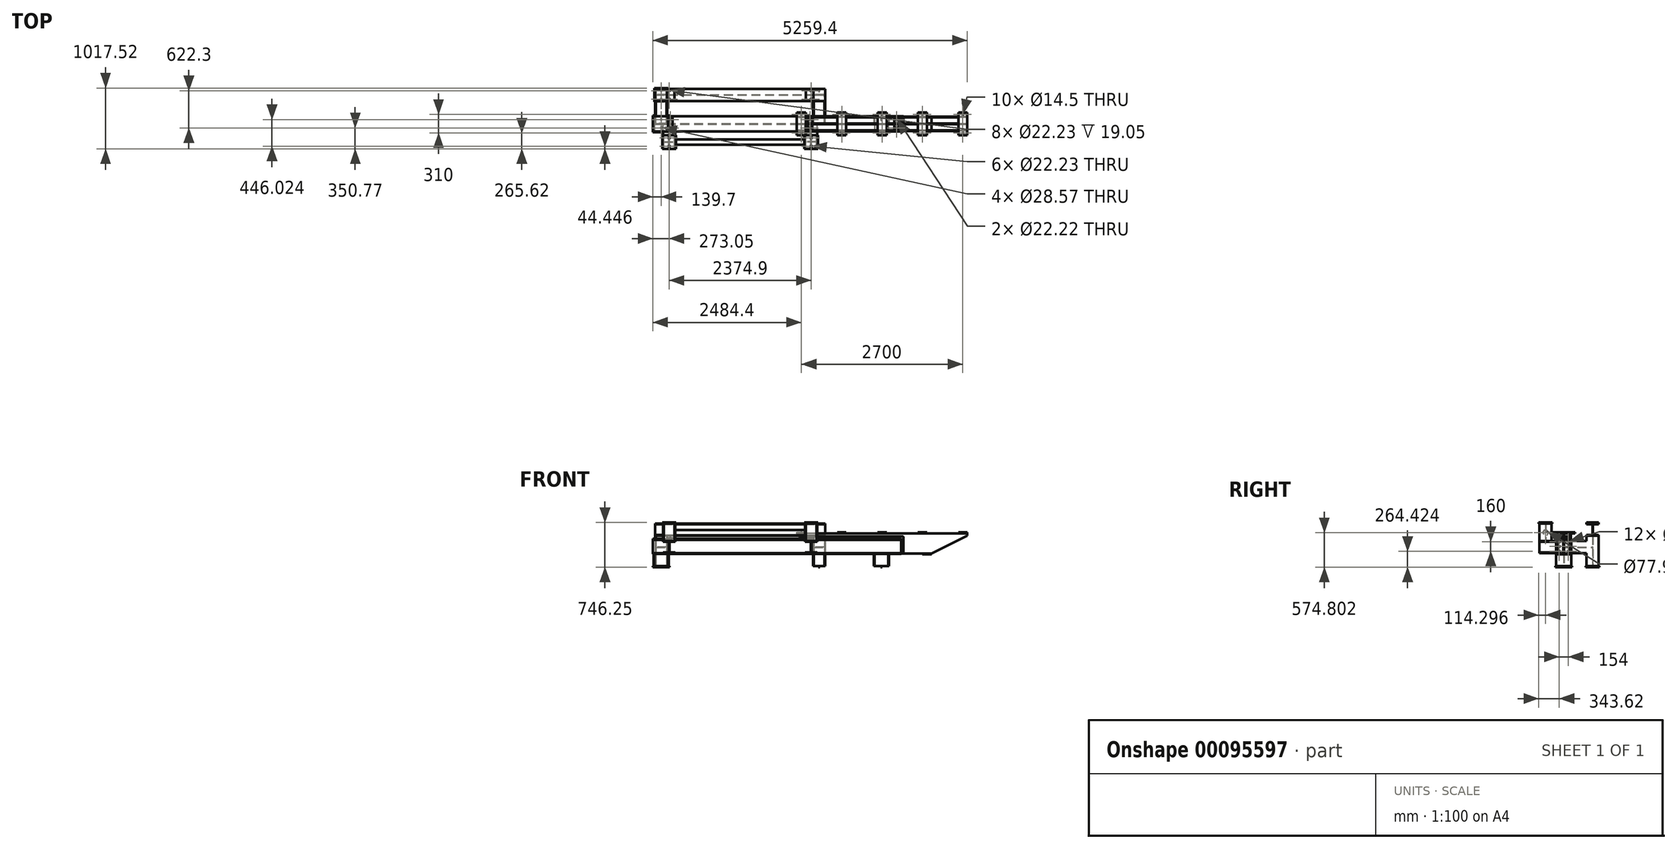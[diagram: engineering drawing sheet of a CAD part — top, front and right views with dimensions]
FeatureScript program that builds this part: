
annotation { "Feature Type Name" : "Feature", "Feature Type Description" : "" }
export const myFeature = defineFeature(function(context is Context, id is Id, definition is map)
    precondition{}
    {
        {
            var Q0;
            Q0=qCreatedBy(makeId("Top.planeOp"),FACE);
            var sketch = newSketch(context, id + "F0", { "sketchPlane" : qUnion([Q0])});
            skLineSegment(sketch, "E0.bottom", {"start": v(-1320.8, 241.3) * mm, "end": v(1320.8, 241.3) * mm, "construction": true});
            skLineSegment(sketch, "E0.top", {"start": v(-1320.8, -241.3) * mm, "end": v(1320.8, -241.3) * mm, "construction": true});
            skLineSegment(sketch, "E0.left", {"start": v(-1320.8, 241.3) * mm, "end": v(-1320.8, -241.3) * mm, "construction": true});
            skLineSegment(sketch, "E0.right", {"start": v(1320.8, 241.3) * mm, "end": v(1320.8, -241.3) * mm, "construction": true});
            skPoint(sketch, "E0.middle", {"position": v(0, 0) * mm});
            skLineSegment(sketch, "E1.bottom", {"start": v(-1435.1, 355.6) * mm, "end": v(-1206.5, 355.6) * mm});
            skLineSegment(sketch, "E1.top", {"start": v(-1435.1, 127) * mm, "end": v(-1206.5, 127) * mm});
            skLineSegment(sketch, "E1.left", {"start": v(-1435.1, 355.6) * mm, "end": v(-1435.1, 127) * mm});
            skLineSegment(sketch, "E1.right", {"start": v(-1206.5, 355.6) * mm, "end": v(-1206.5, 127) * mm});
            skPoint(sketch, "E1.middle", {"position": v(-1320.8, 241.3) * mm});
            skLineSegment(sketch, "E2", {"start": v(0, -413.23) * mm, "end": v(0, 639.03) * mm, "construction": true});
            skLineSegment(sketch, "E3", {"start": v(-1320.8, 355.6) * mm, "end": v(-1320.8, 127) * mm, "construction": true});
            skLineSegment(sketch, "E4", {"start": v(-1435.1, 241.3) * mm, "end": v(-1206.5, 241.3) * mm, "construction": true});
            skLineSegment(sketch, "E5.0", {"start": v(-1435.1, 311.15) * mm, "end": v(-1206.5, 311.15) * mm, "construction": true});
            skCircle(sketch, "E6", {"center": v(-1320.8, 311.15) * mm, "radius": 14.29 * mm});
            skCircle(sketch, "E7.MirrorC", {"center": v(-1320.8, 171.45) * mm, "radius": 14.29 * mm});
            skCircle(sketch, "E8.MirrorC", {"center": v(1320.8, 311.15) * mm, "radius": 14.29 * mm});
            skCircle(sketch, "E9.MirrorC", {"center": v(1320.8, 171.45) * mm, "radius": 14.29 * mm});
            skLineSegment(sketch, "E10.MirrorCS", {"start": v(1435.1, 311.15) * mm, "end": v(1206.5, 311.15) * mm, "construction": true});
            skLineSegment(sketch, "E11.MirrorCS", {"start": v(1435.1, 241.3) * mm, "end": v(1206.5, 241.3) * mm, "construction": true});
            skLineSegment(sketch, "E12.MirrorCS", {"start": v(1320.8, 355.6) * mm, "end": v(1320.8, 127) * mm, "construction": true});
            skLineSegment(sketch, "E13.MirrorCS", {"start": v(1435.1, 355.6) * mm, "end": v(1206.5, 355.6) * mm});
            skPoint(sketch, "E14.MirrorP", {"position": v(1320.8, 241.3) * mm});
            skLineSegment(sketch, "E15.MirrorCS", {"start": v(1206.5, 355.6) * mm, "end": v(1206.5, 127) * mm});
            skLineSegment(sketch, "E16.MirrorCS", {"start": v(1435.1, 127) * mm, "end": v(1206.5, 127) * mm});
            skLineSegment(sketch, "E17.MirrorCS", {"start": v(1435.1, 355.6) * mm, "end": v(1435.1, 127) * mm});
            skLineSegment(sketch, "E18.bottom", {"start": v(-1460.5, -381) * mm, "end": v(-1181.1, -381) * mm});
            skLineSegment(sketch, "E18.top", {"start": v(-1460.5, -101.6) * mm, "end": v(-1181.1, -101.6) * mm});
            skLineSegment(sketch, "E18.left", {"start": v(-1460.5, -381) * mm, "end": v(-1460.5, -101.6) * mm});
            skLineSegment(sketch, "E18.right", {"start": v(-1181.1, -381) * mm, "end": v(-1181.1, -101.6) * mm});
            skPoint(sketch, "E18.middle", {"position": v(-1320.8, -241.3) * mm});
            skLineSegment(sketch, "E19", {"start": v(-1320.8, -241.3) * mm, "end": v(-1460.5, -241.3) * mm, "construction": true});
            skLineSegment(sketch, "E20.0", {"start": v(-1320.8, -171.45) * mm, "end": v(-1460.5, -171.45) * mm, "construction": true});
            skCircle(sketch, "E21", {"center": v(-1320.8, -171.45) * mm, "radius": 14.29 * mm});
            skCircle(sketch, "E22.MirrorC", {"center": v(-1320.8, -311.15) * mm, "radius": 14.29 * mm});
            skLineSegment(sketch, "E23", {"start": v(-1320.8, -638.8) * mm, "end": v(-1320.8, -1011) * mm, "construction": true});
            skPoint(sketch, "E24.orphan", {"position": v(-1320.8, -381) * mm});
            skLineSegment(sketch, "E25.0", {"start": v(0, -638.8) * mm, "end": v(0, -1011) * mm, "construction": true});
            skLineSegment(sketch, "E26.0", {"start": v(1320.8, -638.8) * mm, "end": v(1320.8, -1011) * mm, "construction": true});
            skLineSegment(sketch, "E27.0", {"start": v(2362.2, -638.8) * mm, "end": v(2362.2, -1011) * mm, "construction": true});
            skLineSegment(sketch, "E28", {"start": v(-1320.8, -1011) * mm, "end": v(2362.2, -1011) * mm, "construction": true});
            skLineSegment(sketch, "E29", {"start": v(520.7, -1011) * mm, "end": v(520.7, -1354.57) * mm, "construction": true});
            skCircle(sketch, "E30.MirrorC", {"center": v(2362.2, -171.45) * mm, "radius": 14.29 * mm});
            skCircle(sketch, "E31.MirrorC", {"center": v(2362.2, -311.15) * mm, "radius": 14.29 * mm});
            skLineSegment(sketch, "E32.MirrorCS", {"start": v(2362.2, -171.45) * mm, "end": v(2501.9, -171.45) * mm, "construction": true});
            skLineSegment(sketch, "E33.MirrorCS", {"start": v(2501.9, -101.6) * mm, "end": v(2222.5, -101.6) * mm});
            skLineSegment(sketch, "E34.MirrorCS", {"start": v(2501.9, -381) * mm, "end": v(2222.5, -381) * mm});
            skLineSegment(sketch, "E35.MirrorCS", {"start": v(2362.2, -241.3) * mm, "end": v(2501.9, -241.3) * mm, "construction": true});
            skPoint(sketch, "E36.MirrorP", {"position": v(2362.2, -241.3) * mm});
            skLineSegment(sketch, "E37.MirrorCS", {"start": v(2222.5, -381) * mm, "end": v(2222.5, -101.6) * mm});
            skPoint(sketch, "E38.MirrorP", {"position": v(2362.2, -381) * mm});
            skLineSegment(sketch, "E39.MirrorCS", {"start": v(2501.9, -381) * mm, "end": v(2501.9, -101.6) * mm});
            skSolve(sketch);
        }
        {
            var Q0;
            Q0=makeQuery(id+"F0.imprint","IMPRINT",FACE,{"disambiguationData":[TD([[makeQuery(id+"F0.imprint","IMPRINT",EDGE,{"derivedFrom":sQuery(id+"F0.wireOp",EDGE,"E1.bottom")}),-1.0]])]});
            var Q1;
            Q1=makeQuery(id+"F0.imprint","IMPRINT",FACE,{"disambiguationData":[TD([[makeQuery(id+"F0.imprint","IMPRINT",EDGE,{"derivedFrom":sQuery(id+"F0.wireOp",EDGE,"E8.MirrorC")}),1.0]])]});
            var Q2;
            Q2=makeQuery(id+"F0.imprint","IMPRINT",FACE,{"disambiguationData":[TD([[makeQuery(id+"F0.imprint","IMPRINT",EDGE,{"derivedFrom":sQuery(id+"F0.wireOp",EDGE,"E30.MirrorC")}),1.0]])]});
            var Q3;
            Q3=makeQuery(id+"F0.imprint","IMPRINT",FACE,{"disambiguationData":[TD([[makeQuery(id+"F0.imprint","IMPRINT",EDGE,{"derivedFrom":sQuery(id+"F0.wireOp",EDGE,"E18.bottom")}),1.0]])]});
            extrude(context, id + "F1", {"entities" : qUnion([Q0, Q1, Q2, Q3]), "depth" : 19.05 * mm});
        }
        {
            var Q0;
            Q0=makeQuery(id+"F1.opExtrude","CAP_FACE",FACE,{"disambiguationData":[OSD([sQuery(id+"F0.wireOp",EDGE,"E1.bottom"),sQuery(id+"F0.wireOp",EDGE,"E1.top"),sQuery(id+"F0.wireOp",EDGE,"E1.left"),sQuery(id+"F0.wireOp",EDGE,"E1.right"),sQuery(id+"F0.wireOp",EDGE,"E6"),sQuery(id+"F0.wireOp",EDGE,"E7.MirrorC")])],"isStart":false});
            var sketch = newSketch(context, id + "F2", { "sketchPlane" : qUnion([Q0])});
            skLineSegment(sketch, "E40.0", {"start": v(-1435.1, 241.3) * mm, "end": v(-1206.5, 241.3) * mm, "construction": true});
            skLineSegment(sketch, "E41.0", {"start": v(-1320.8, 355.6) * mm, "end": v(-1320.8, 127) * mm, "construction": true});
            skLineSegment(sketch, "E42.bottom", {"start": v(-1422.4, 342.9) * mm, "end": v(-1411.35, 342.9) * mm});
            skLineSegment(sketch, "E42.top", {"start": v(-1422.4, 139.7) * mm, "end": v(-1411.35, 139.7) * mm});
            skLineSegment(sketch, "E42.left", {"start": v(-1422.4, 342.9) * mm, "end": v(-1422.4, 139.7) * mm});
            skLineSegment(sketch, "E42.right", {"start": v(-1219.2, 342.9) * mm, "end": v(-1219.2, 139.7) * mm, "construction": true});
            skPoint(sketch, "E42.middle", {"position": v(-1320.8, 241.3) * mm});
            skLineSegment(sketch, "E43.0", {"start": v(-1411.35, 342.9) * mm, "end": v(-1411.35, 251.27) * mm});
            skLineSegment(sketch, "E44.trimOffspring", {"start": v(-1405, 237.68) * mm, "end": v(-1320.8, 237.68) * mm});
            skLineSegment(sketch, "E45.MirrorCS", {"start": v(-1405, 244.92) * mm, "end": v(-1320.8, 244.92) * mm});
            skLineSegment(sketch, "E46.trimOffspring", {"start": v(-1411.35, 231.33) * mm, "end": v(-1411.35, 139.7) * mm});
            skPoint(sketch, "E47.visualSharp", {"position": v(-1411.35, 244.92) * mm});
            skArc(sketch, "E47.filletArc", {"start": v(-1411.35, 251.27) * mm, "mid": v(-1409.5, 246.78) * mm, "end": v(-1405, 244.92) * mm});
            skPoint(sketch, "E48.visualSharp", {"position": v(-1411.35, 237.68) * mm});
            skArc(sketch, "E48.filletArc", {"start": v(-1405, 237.68) * mm, "mid": v(-1409.5, 235.82) * mm, "end": v(-1411.35, 231.33) * mm});
            skArc(sketch, "E49.MirrorCS", {"start": v(-1236.6, 237.68) * mm, "mid": v(-1232.1, 235.82) * mm, "end": v(-1230.25, 231.33) * mm});
            skArc(sketch, "E50.MirrorCS", {"start": v(-1230.25, 251.27) * mm, "mid": v(-1232.1, 246.78) * mm, "end": v(-1236.6, 244.92) * mm});
            skPoint(sketch, "E51.MirrorP", {"position": v(-1230.25, 237.68) * mm});
            skPoint(sketch, "E52.MirrorP", {"position": v(-1230.25, 244.92) * mm});
            skLineSegment(sketch, "E53.MirrorCS", {"start": v(-1230.25, 342.9) * mm, "end": v(-1230.25, 251.27) * mm});
            skLineSegment(sketch, "E54.MirrorCS", {"start": v(-1236.6, 237.68) * mm, "end": v(-1320.8, 237.68) * mm});
            skLineSegment(sketch, "E55.MirrorCS", {"start": v(-1236.6, 244.92) * mm, "end": v(-1320.8, 244.92) * mm});
            skLineSegment(sketch, "E56.MirrorCS", {"start": v(-1219.2, 139.7) * mm, "end": v(-1230.25, 139.7) * mm});
            skLineSegment(sketch, "E57.MirrorCS", {"start": v(-1230.25, 231.33) * mm, "end": v(-1230.25, 139.7) * mm});
            skLineSegment(sketch, "E58.MirrorCS", {"start": v(-1219.2, 342.9) * mm, "end": v(-1230.25, 342.9) * mm});
            skLineSegment(sketch, "E59.MirrorCS", {"start": v(-1219.2, 342.9) * mm, "end": v(-1219.2, 139.7) * mm});
            skLineSegment(sketch, "E60.0", {"start": v(0, -413.23) * mm, "end": v(0, 639.03) * mm, "construction": true});
            skArc(sketch, "E61.MirrorCS", {"start": v(1411.35, 251.27) * mm, "mid": v(1409.5, 246.78) * mm, "end": v(1405, 244.92) * mm});
            skArc(sketch, "E62.MirrorCS", {"start": v(1405, 237.68) * mm, "mid": v(1409.5, 235.82) * mm, "end": v(1411.35, 231.33) * mm});
            skLineSegment(sketch, "E63.MirrorCS", {"start": v(1236.6, 244.92) * mm, "end": v(1320.8, 244.92) * mm});
            skArc(sketch, "E64.MirrorCS", {"start": v(1236.6, 237.68) * mm, "mid": v(1232.1, 235.82) * mm, "end": v(1230.25, 231.33) * mm});
            skLineSegment(sketch, "E65.MirrorCS", {"start": v(1422.4, 139.7) * mm, "end": v(1411.35, 139.7) * mm});
            skLineSegment(sketch, "E66.MirrorCS", {"start": v(1422.4, 342.9) * mm, "end": v(1411.35, 342.9) * mm});
            skArc(sketch, "E67.MirrorCS", {"start": v(1230.25, 251.27) * mm, "mid": v(1232.1, 246.78) * mm, "end": v(1236.6, 244.92) * mm});
            skLineSegment(sketch, "E68.MirrorCS", {"start": v(1236.6, 237.68) * mm, "end": v(1320.8, 237.68) * mm});
            skLineSegment(sketch, "E69.MirrorCS", {"start": v(1435.1, 241.3) * mm, "end": v(1206.5, 241.3) * mm, "construction": true});
            skLineSegment(sketch, "E70.MirrorCS", {"start": v(1405, 237.68) * mm, "end": v(1320.8, 237.68) * mm});
            skLineSegment(sketch, "E71.MirrorCS", {"start": v(1219.2, 342.9) * mm, "end": v(1230.25, 342.9) * mm});
            skLineSegment(sketch, "E72.MirrorCS", {"start": v(1219.2, 139.7) * mm, "end": v(1230.25, 139.7) * mm});
            skLineSegment(sketch, "E73.MirrorCS", {"start": v(1411.35, 342.9) * mm, "end": v(1411.35, 251.27) * mm});
            skLineSegment(sketch, "E74.MirrorCS", {"start": v(1405, 244.92) * mm, "end": v(1320.8, 244.92) * mm});
            skLineSegment(sketch, "E75.MirrorCS", {"start": v(1411.35, 231.33) * mm, "end": v(1411.35, 139.7) * mm});
            skPoint(sketch, "E76.MirrorP", {"position": v(1411.35, 237.68) * mm});
            skPoint(sketch, "E77.MirrorP", {"position": v(1320.8, 241.3) * mm});
            skLineSegment(sketch, "E78.MirrorCS", {"start": v(1219.2, 342.9) * mm, "end": v(1219.2, 139.7) * mm, "construction": true});
            skLineSegment(sketch, "E79.MirrorCS", {"start": v(1422.4, 342.9) * mm, "end": v(1422.4, 139.7) * mm});
            skPoint(sketch, "E80.MirrorP", {"position": v(1230.25, 237.68) * mm});
            skLineSegment(sketch, "E81.MirrorCS", {"start": v(1320.8, 355.6) * mm, "end": v(1320.8, 127) * mm, "construction": true});
            skPoint(sketch, "E82.MirrorP", {"position": v(1411.35, 244.92) * mm});
            skLineSegment(sketch, "E83.MirrorCS", {"start": v(1219.2, 342.9) * mm, "end": v(1219.2, 139.7) * mm});
            skLineSegment(sketch, "E84.MirrorCS", {"start": v(1230.25, 231.33) * mm, "end": v(1230.25, 139.7) * mm});
            skLineSegment(sketch, "E85.MirrorCS", {"start": v(1230.25, 342.9) * mm, "end": v(1230.25, 251.27) * mm});
            skPoint(sketch, "E86.MirrorP", {"position": v(1230.25, 244.92) * mm});
            skSolve(sketch);
        }
        {
            var Q0;
            Q0=qSketchRegion(id+"F2",true);
            extrude(context, id + "F3", {"entities" : qUnion([Q0]), "depth" : 504.95 * mm});
        }
        {
            var Q0;
            Q0=makeQuery(id+"F3.opExtrude","SWEPT_FACE",FACE,{"disambiguationData":[OSD([sQuery(id+"F2.wireOp",EDGE,"E79.MirrorCS")])]});
            var sketch = newSketch(context, id + "F4", { "sketchPlane" : qUnion([Q0])});
            skLineSegment(sketch, "E87.bottom", {"start": v(139.7, 524) * mm, "end": v(342.9, 524) * mm});
            skLineSegment(sketch, "E87.top", {"start": v(139.7, 727.2) * mm, "end": v(342.9, 727.2) * mm});
            skLineSegment(sketch, "E87.left", {"start": v(139.7, 524) * mm, "end": v(139.7, 535.05) * mm});
            skLineSegment(sketch, "E87.right", {"start": v(342.9, 524) * mm, "end": v(342.9, 535.05) * mm});
            skLineSegment(sketch, "E88", {"start": v(241.3, 727.2) * mm, "end": v(241.3, 524) * mm, "construction": true});
            skLineSegment(sketch, "E89.0", {"start": v(237.68, 709.8) * mm, "end": v(237.68, 541.4) * mm});
            skLineSegment(sketch, "E90.MirrorCS", {"start": v(244.92, 709.8) * mm, "end": v(244.92, 541.4) * mm});
            skLineSegment(sketch, "E91.0", {"start": v(139.7, 716.15) * mm, "end": v(231.33, 716.15) * mm});
            skLineSegment(sketch, "E92.0", {"start": v(139.7, 535.05) * mm, "end": v(231.33, 535.05) * mm});
            skLineSegment(sketch, "E93.trimOffspring", {"start": v(251.27, 716.15) * mm, "end": v(342.9, 716.15) * mm});
            skLineSegment(sketch, "E94.trimOffspring", {"start": v(251.27, 535.05) * mm, "end": v(342.9, 535.05) * mm});
            skLineSegment(sketch, "E95.trimOffspring", {"start": v(139.7, 716.15) * mm, "end": v(139.7, 727.2) * mm});
            skLineSegment(sketch, "E96.trimOffspring", {"start": v(342.9, 716.15) * mm, "end": v(342.9, 727.2) * mm});
            skPoint(sketch, "E97.newPointB", {"position": v(237.68, 524) * mm});
            skArc(sketch, "E97.filletArc", {"start": v(231.33, 535.05) * mm, "mid": v(235.82, 536.91) * mm, "end": v(237.68, 541.4) * mm});
            skPoint(sketch, "E98.newPointA", {"position": v(244.92, 524) * mm});
            skArc(sketch, "E98.filletArc", {"start": v(244.92, 541.4) * mm, "mid": v(246.78, 536.91) * mm, "end": v(251.27, 535.05) * mm});
            skPoint(sketch, "E99.newPointA", {"position": v(237.68, 727.2) * mm});
            skArc(sketch, "E99.filletArc", {"start": v(237.68, 709.8) * mm, "mid": v(235.82, 714.3) * mm, "end": v(231.33, 716.15) * mm});
            skPoint(sketch, "E100.newPointA", {"position": v(244.92, 727.2) * mm});
            skArc(sketch, "E100.filletArc", {"start": v(251.27, 716.15) * mm, "mid": v(246.78, 714.3) * mm, "end": v(244.92, 709.8) * mm});
            skSolve(sketch);
        }
        {
            var Q0;
            Q0=qSketchRegion(id+"F4",true);
            var Q1;
            Q1=makeQuery(id+"F3.opExtrude","SWEPT_FACE",FACE,{"disambiguationData":[OSD([sQuery(id+"F2.wireOp",EDGE,"E42.left")])]});
            extrude(context, id + "F5", {"entities" : qUnion([Q0]), "endBound" : BoundingType.UP_TO_SURFACE, "oppositeDirection" : true, "endBoundEntityFace" : qUnion([Q1]), "depth" : 25.4 * mm});
        }
        {
            var Q0;
            Q0=makeQuery(id+"F5.opExtrude","SWEPT_FACE",FACE,{"disambiguationData":[OSD([sQuery(id+"F4.wireOp",EDGE,"E87.top")])]});
            var sketch = newSketch(context, id + "F6", { "sketchPlane" : qUnion([Q0])});
            skLineSegment(sketch, "E101.0", {"start": v(0, -413.23) * mm, "end": v(0, 639.03) * mm, "construction": true});
            skLineSegment(sketch, "E102.0", {"start": v(-1187.45, -413.23) * mm, "end": v(-1187.45, 639.03) * mm, "construction": true});
            skLineSegment(sketch, "E103.0", {"start": v(-1225.55, 139.7) * mm, "end": v(-1225.55, 342.9) * mm});
            skLineSegment(sketch, "E104.0", {"start": v(-1098.55, 139.7) * mm, "end": v(-1098.55, 342.9) * mm});
            skLineSegment(sketch, "E105.0", {"start": v(-1422.4, 342.9) * mm, "end": v(1422.4, 342.9) * mm, "construction": true});
            skLineSegment(sketch, "E106.0.0", {"start": v(1225.55, 342.9) * mm, "end": v(-1225.55, 342.9) * mm});
            skLineSegment(sketch, "E106.0.1", {"start": v(-1422.4, 342.9) * mm, "end": v(-1422.4, 139.7) * mm});
            skLineSegment(sketch, "E106.0.2", {"start": v(-1225.55, 139.7) * mm, "end": v(-1098.55, 139.7) * mm});
            skLineSegment(sketch, "E106.0.3", {"start": v(1422.4, 139.7) * mm, "end": v(1422.4, 342.9) * mm});
            skLineSegment(sketch, "E107.trimOffspring", {"start": v(0, 139.7) * mm, "end": v(1225.55, 139.7) * mm});
            skLineSegment(sketch, "E108.0", {"start": v(-1320.8, 241.3) * mm, "end": v(1320.8, 241.3) * mm, "construction": true});
            skLineSegment(sketch, "E109.0", {"start": v(-1320.8, 311.15) * mm, "end": v(1320.8, 311.15) * mm, "construction": true});
            skCircle(sketch, "E110", {"center": v(-1187.45, 311.15) * mm, "radius": 11.11 * mm});
            skCircle(sketch, "E111.MirrorC", {"center": v(-1187.45, 171.45) * mm, "radius": 11.11 * mm});
            skCircle(sketch, "E112.MirrorC", {"center": v(1187.45, 311.15) * mm, "radius": 11.11 * mm});
            skCircle(sketch, "E113.MirrorC", {"center": v(1187.45, 171.45) * mm, "radius": 11.11 * mm});
            skLineSegment(sketch, "E114.MirrorCS", {"start": v(1225.55, 139.7) * mm, "end": v(1098.55, 139.7) * mm});
            skLineSegment(sketch, "E115.MirrorCS", {"start": v(1225.55, 139.7) * mm, "end": v(1225.55, 342.9) * mm});
            skLineSegment(sketch, "E116.MirrorCS", {"start": v(1098.55, 139.7) * mm, "end": v(1098.55, 342.9) * mm});
            skSolve(sketch);
        }
        {
            var Q0;
            Q0=qSketchRegion(id+"F6",true);
            extrude(context, id + "F7", {"entities" : qUnion([Q0]), "operationType" : NewBodyOperationType.ADD, "depth" : 19.05 * mm});
        }
        {
            var Q0;
            Q0=makeQuery(id+"F3.opExtrude","SWEPT_FACE",FACE,{"disambiguationData":[OSD([sQuery(id+"F2.wireOp",EDGE,"E44.trimOffspring"),sQuery(id+"F2.wireOp",EDGE,"E54.MirrorCS")])]});
            var sketch = newSketch(context, id + "F8", { "sketchPlane" : qUnion([Q0])});
            skLineSegment(sketch, "E117.0", {"start": v(-1460.5, 0) * mm, "end": v(-1181.1, 0) * mm, "construction": true});
            skLineSegment(sketch, "E118", {"start": v(-1320.8, 0) * mm, "end": v(-1320.8, 868.41) * mm, "construction": true});
            skLineSegment(sketch, "E119.0", {"start": v(-1422.4, 231.65) * mm, "end": v(-1411.35, 231.65) * mm});
            skLineSegment(sketch, "E120.0", {"start": v(-1422.4, 434.85) * mm, "end": v(-1411.35, 434.85) * mm});
            skLineSegment(sketch, "E121", {"start": v(-1422.4, 434.85) * mm, "end": v(-1422.4, 231.65) * mm});
            skLineSegment(sketch, "E122.0", {"start": v(-1411.35, 434.85) * mm, "end": v(-1411.35, 342.77) * mm});
            skLineSegment(sketch, "E123", {"start": v(-1411.35, 333.25) * mm, "end": v(-1320.8, 333.25) * mm, "construction": true});
            skLineSegment(sketch, "E124.0", {"start": v(-1405, 336.42) * mm, "end": v(-1320.8, 336.42) * mm});
            skLineSegment(sketch, "E125.MirrorCS", {"start": v(-1410.08, 330.07) * mm, "end": v(-1320.8, 330.07) * mm});
            skLineSegment(sketch, "E126.trimOffspring", {"start": v(-1411.35, 328.8) * mm, "end": v(-1411.35, 231.65) * mm});
            skPoint(sketch, "E127.newPointA", {"position": v(-1411.35, 336.42) * mm});
            skArc(sketch, "E127.filletArc", {"start": v(-1411.35, 342.77) * mm, "mid": v(-1409.5, 338.28) * mm, "end": v(-1405, 336.42) * mm});
            skPoint(sketch, "E128.visualSharp", {"position": v(-1411.35, 330.07) * mm});
            skArc(sketch, "E128.filletArc", {"start": v(-1410.08, 330.07) * mm, "mid": v(-1410.98, 329.7) * mm, "end": v(-1411.35, 328.8) * mm});
            skArc(sketch, "E129.MirrorCS", {"start": v(-1231.52, 330.07) * mm, "mid": v(-1230.62, 329.7) * mm, "end": v(-1230.25, 328.8) * mm});
            skArc(sketch, "E130.MirrorCS", {"start": v(-1230.25, 342.77) * mm, "mid": v(-1232.1, 338.28) * mm, "end": v(-1236.6, 336.42) * mm});
            skLineSegment(sketch, "E131.MirrorCS", {"start": v(-1219.2, 231.65) * mm, "end": v(-1230.25, 231.65) * mm});
            skLineSegment(sketch, "E132.MirrorCS", {"start": v(-1219.2, 434.85) * mm, "end": v(-1230.25, 434.85) * mm});
            skPoint(sketch, "E133.MirrorP", {"position": v(-1230.25, 336.42) * mm});
            skPoint(sketch, "E134.MirrorP", {"position": v(-1230.25, 330.07) * mm});
            skLineSegment(sketch, "E135.MirrorCS", {"start": v(-1230.25, 328.8) * mm, "end": v(-1230.25, 231.65) * mm});
            skLineSegment(sketch, "E136.MirrorCS", {"start": v(-1231.52, 330.07) * mm, "end": v(-1320.8, 330.07) * mm});
            skLineSegment(sketch, "E137.MirrorCS", {"start": v(-1219.2, 434.85) * mm, "end": v(-1219.2, 231.65) * mm});
            skLineSegment(sketch, "E138.MirrorCS", {"start": v(-1230.25, 434.85) * mm, "end": v(-1230.25, 342.77) * mm});
            skLineSegment(sketch, "E139.MirrorCS", {"start": v(-1230.25, 333.25) * mm, "end": v(-1320.8, 333.25) * mm, "construction": true});
            skLineSegment(sketch, "E140.MirrorCS", {"start": v(-1236.6, 336.42) * mm, "end": v(-1320.8, 336.42) * mm});
            skLineSegment(sketch, "E141", {"start": v(0, -179.83) * mm, "end": v(0, 965.66) * mm, "construction": true});
            skArc(sketch, "E142.MirrorCS", {"start": v(1411.35, 342.77) * mm, "mid": v(1409.5, 338.28) * mm, "end": v(1405, 336.42) * mm});
            skArc(sketch, "E143.MirrorCS", {"start": v(1410.08, 330.07) * mm, "mid": v(1410.98, 329.7) * mm, "end": v(1411.35, 328.8) * mm});
            skArc(sketch, "E144.MirrorCS", {"start": v(1230.25, 342.77) * mm, "mid": v(1232.1, 338.28) * mm, "end": v(1236.6, 336.42) * mm});
            skArc(sketch, "E145.MirrorCS", {"start": v(1231.52, 330.07) * mm, "mid": v(1230.62, 329.7) * mm, "end": v(1230.25, 328.8) * mm});
            skLineSegment(sketch, "E146.MirrorCS", {"start": v(1411.35, 333.25) * mm, "end": v(1320.8, 333.25) * mm, "construction": true});
            skLineSegment(sketch, "E147.MirrorCS", {"start": v(1219.2, 231.65) * mm, "end": v(1230.25, 231.65) * mm});
            skLineSegment(sketch, "E148.MirrorCS", {"start": v(1219.2, 434.85) * mm, "end": v(1230.25, 434.85) * mm});
            skLineSegment(sketch, "E149.MirrorCS", {"start": v(1422.4, 231.65) * mm, "end": v(1411.35, 231.65) * mm});
            skLineSegment(sketch, "E150.MirrorCS", {"start": v(1422.4, 434.85) * mm, "end": v(1411.35, 434.85) * mm});
            skLineSegment(sketch, "E151.MirrorCS", {"start": v(1405, 336.42) * mm, "end": v(1320.8, 336.42) * mm});
            skLineSegment(sketch, "E152.MirrorCS", {"start": v(1410.08, 330.07) * mm, "end": v(1320.8, 330.07) * mm});
            skLineSegment(sketch, "E153.MirrorCS", {"start": v(1230.25, 333.25) * mm, "end": v(1320.8, 333.25) * mm, "construction": true});
            skLineSegment(sketch, "E154.MirrorCS", {"start": v(1231.52, 330.07) * mm, "end": v(1320.8, 330.07) * mm});
            skLineSegment(sketch, "E155.MirrorCS", {"start": v(1236.6, 336.42) * mm, "end": v(1320.8, 336.42) * mm});
            skLineSegment(sketch, "E156.MirrorCS", {"start": v(1411.35, 328.8) * mm, "end": v(1411.35, 231.65) * mm});
            skPoint(sketch, "E157.MirrorP", {"position": v(1411.35, 330.07) * mm});
            skPoint(sketch, "E158.MirrorP", {"position": v(1411.35, 336.42) * mm});
            skLineSegment(sketch, "E159.MirrorCS", {"start": v(1422.4, 434.85) * mm, "end": v(1422.4, 231.65) * mm});
            skLineSegment(sketch, "E160.MirrorCS", {"start": v(1411.35, 434.85) * mm, "end": v(1411.35, 342.77) * mm});
            skLineSegment(sketch, "E161.MirrorCS", {"start": v(1230.25, 434.85) * mm, "end": v(1230.25, 342.77) * mm});
            skLineSegment(sketch, "E162.MirrorCS", {"start": v(1230.25, 328.8) * mm, "end": v(1230.25, 231.65) * mm});
            skPoint(sketch, "E163.MirrorP", {"position": v(1230.25, 330.07) * mm});
            skPoint(sketch, "E164.MirrorP", {"position": v(1230.25, 336.42) * mm});
            skLineSegment(sketch, "E165.MirrorCS", {"start": v(1219.2, 434.85) * mm, "end": v(1219.2, 231.65) * mm});
            skSolve(sketch);
        }
        {
            var Q0;
            Q0=qSketchRegion(id+"F8",true);
            extrude(context, id + "F9", {"entities" : qUnion([Q0]), "operationType" : NewBodyOperationType.ADD, "depth" : 482.6 * mm});
        }
        {
            var Q0;
            Q0=qCreatedBy(makeId("Right.planeOp"),FACE);
            cPlane(context, id + "F10", {"entities" : qUnion([Q0]), "cplaneType" : CPlaneType.OFFSET, "offset" : 2692.4 * mm, "width" : 152.4 * mm, "height" : 152.4 * mm});
        }
        {
            var Q0;
            Q0=qCreatedBy(id+"F10.planeOp",FACE);
            var sketch = newSketch(context, id + "F11", { "sketchPlane" : qUnion([Q0])});
            skLineSegment(sketch, "E166.0", {"start": v(-381, 19.05) * mm, "end": v(-101.6, 19.05) * mm, "construction": true});
            skLineSegment(sketch, "E167", {"start": v(-241.3, 19.05) * mm, "end": v(-241.3, 468.37) * mm, "construction": true});
            skLineSegment(sketch, "E168.0", {"start": v(-381, 217.42) * mm, "end": v(-101.6, 217.42) * mm, "construction": true});
            skLineSegment(sketch, "E169.bottom", {"start": v(-368.3, 217.42) * mm, "end": v(-114.3, 217.42) * mm});
            skLineSegment(sketch, "E169.top", {"start": v(-368.3, 471.42) * mm, "end": v(-114.3, 471.42) * mm});
            skLineSegment(sketch, "E169.left", {"start": v(-368.3, 217.42) * mm, "end": v(-368.3, 231.65) * mm});
            skLineSegment(sketch, "E169.right", {"start": v(-114.3, 217.42) * mm, "end": v(-114.3, 231.65) * mm});
            skLineSegment(sketch, "E170.0", {"start": v(-368.3, 457.2) * mm, "end": v(-254, 457.2) * mm});
            skLineSegment(sketch, "E171.0", {"start": v(-368.3, 231.65) * mm, "end": v(-254, 231.65) * mm});
            skLineSegment(sketch, "E172.0", {"start": v(-234.95, 238) * mm, "end": v(-234.95, 450.85) * mm});
            skLineSegment(sketch, "E173.MirrorCS", {"start": v(-247.65, 238) * mm, "end": v(-247.65, 450.85) * mm});
            skLineSegment(sketch, "E174.trimOffspring", {"start": v(-368.3, 457.2) * mm, "end": v(-368.3, 471.42) * mm});
            skLineSegment(sketch, "E175.trimOffspring", {"start": v(-114.3, 457.2) * mm, "end": v(-114.3, 471.42) * mm});
            skLineSegment(sketch, "E176.trimOffspring", {"start": v(-228.6, 457.2) * mm, "end": v(-114.3, 457.2) * mm});
            skLineSegment(sketch, "E177.trimOffspring", {"start": v(-228.6, 231.65) * mm, "end": v(-114.3, 231.65) * mm});
            skPoint(sketch, "E178.newPointB", {"position": v(-247.65, 468.37) * mm});
            skArc(sketch, "E178.filletArc", {"start": v(-247.65, 450.85) * mm, "mid": v(-249.5, 455.34) * mm, "end": v(-254, 457.2) * mm});
            skPoint(sketch, "E179.newPointB", {"position": v(-234.95, 468.37) * mm});
            skArc(sketch, "E179.filletArc", {"start": v(-228.6, 457.2) * mm, "mid": v(-233.1, 455.34) * mm, "end": v(-234.95, 450.85) * mm});
            skPoint(sketch, "E180.newPointB", {"position": v(-234.95, 19.05) * mm});
            skArc(sketch, "E180.filletArc", {"start": v(-234.95, 238) * mm, "mid": v(-233.1, 233.5) * mm, "end": v(-228.6, 231.65) * mm});
            skPoint(sketch, "E181.newPointA", {"position": v(-247.65, 19.05) * mm});
            skArc(sketch, "E181.filletArc", {"start": v(-254, 231.65) * mm, "mid": v(-249.5, 233.5) * mm, "end": v(-247.65, 238) * mm});
            skSolve(sketch);
        }
        {
            var Q0;
            Q0=qSketchRegion(id+"F11",true);
            extrude(context, id + "F12", {"entities" : qUnion([Q0]), "oppositeDirection" : true, "depth" : 4152.9 * mm});
        }
        {
            var Q0;
            Q0=makeQuery(id+"F1.opExtrude","CAP_FACE",FACE,{"disambiguationData":[OSD([sQuery(id+"F0.wireOp",EDGE,"E18.bottom"),sQuery(id+"F0.wireOp",EDGE,"E18.top"),sQuery(id+"F0.wireOp",EDGE,"E18.left"),sQuery(id+"F0.wireOp",EDGE,"E18.right"),sQuery(id+"F0.wireOp",EDGE,"E21"),sQuery(id+"F0.wireOp",EDGE,"E22.MirrorC")])],"isStart":false});
            var sketch = newSketch(context, id + "F13", { "sketchPlane" : qUnion([Q0])});
            skLineSegment(sketch, "E182.bottom", {"start": v(-1447.8, -114.3) * mm, "end": v(-1433.58, -114.3) * mm});
            skLineSegment(sketch, "E182.top", {"start": v(-1447.8, -368.3) * mm, "end": v(-1433.58, -368.3) * mm});
            skLineSegment(sketch, "E182.left", {"start": v(-1447.8, -114.3) * mm, "end": v(-1447.8, -368.3) * mm});
            skLineSegment(sketch, "E182.right", {"start": v(-1193.8, -114.3) * mm, "end": v(-1193.8, -368.3) * mm});
            skPoint(sketch, "E182.middle", {"position": v(-1320.8, -241.3) * mm});
            skLineSegment(sketch, "E183.0", {"start": v(-1433.58, -114.3) * mm, "end": v(-1433.58, -236.98) * mm});
            skLineSegment(sketch, "E184.0", {"start": v(-1208.02, -114.3) * mm, "end": v(-1208.02, -236.98) * mm});
            skLineSegment(sketch, "E185.trimOffspring", {"start": v(-1208.02, -114.3) * mm, "end": v(-1193.8, -114.3) * mm});
            skLineSegment(sketch, "E186.trimOffspring", {"start": v(-1208.02, -368.3) * mm, "end": v(-1193.8, -368.3) * mm});
            skLineSegment(sketch, "E187.0", {"start": v(-1208.02, -236.98) * mm, "end": v(-1433.58, -236.98) * mm});
            skLineSegment(sketch, "E188.MirrorCS", {"start": v(-1208.02, -245.62) * mm, "end": v(-1433.58, -245.62) * mm});
            skPoint(sketch, "E189.orphan", {"position": v(-1460.5, -236.98) * mm});
            skPoint(sketch, "E190.orphan", {"position": v(-1460.5, -245.62) * mm});
            skLineSegment(sketch, "E191.trimOffspring", {"start": v(-1433.58, -245.62) * mm, "end": v(-1433.58, -368.3) * mm});
            skPoint(sketch, "E192.orphan", {"position": v(-1320.8, -236.98) * mm});
            skPoint(sketch, "E193.orphan", {"position": v(-1320.8, -245.62) * mm});
            skLineSegment(sketch, "E194.trimOffspring", {"start": v(-1208.02, -245.62) * mm, "end": v(-1208.02, -368.3) * mm});
            skLineSegment(sketch, "E195.MirrorCS", {"start": v(2489.2, -368.3) * mm, "end": v(2474.98, -368.3) * mm});
            skLineSegment(sketch, "E196.MirrorCS", {"start": v(2489.2, -114.3) * mm, "end": v(2474.98, -114.3) * mm});
            skLineSegment(sketch, "E197.MirrorCS", {"start": v(2249.42, -368.3) * mm, "end": v(2235.2, -368.3) * mm});
            skLineSegment(sketch, "E198.MirrorCS", {"start": v(2249.42, -114.3) * mm, "end": v(2235.2, -114.3) * mm});
            skPoint(sketch, "E199.MirrorP", {"position": v(2362.2, -245.62) * mm});
            skPoint(sketch, "E200.MirrorP", {"position": v(2362.2, -236.98) * mm});
            skLineSegment(sketch, "E201.MirrorCS", {"start": v(2249.42, -245.62) * mm, "end": v(2474.98, -245.62) * mm});
            skPoint(sketch, "E202.MirrorP", {"position": v(2501.9, -236.98) * mm});
            skLineSegment(sketch, "E203.MirrorCS", {"start": v(2249.42, -236.98) * mm, "end": v(2474.98, -236.98) * mm});
            skPoint(sketch, "E204.MirrorP", {"position": v(2362.2, -241.3) * mm});
            skPoint(sketch, "E205.MirrorP", {"position": v(2501.9, -245.62) * mm});
            skLineSegment(sketch, "E206.MirrorCS", {"start": v(2249.42, -245.62) * mm, "end": v(2249.42, -368.3) * mm});
            skLineSegment(sketch, "E207.MirrorCS", {"start": v(2474.98, -245.62) * mm, "end": v(2474.98, -368.3) * mm});
            skLineSegment(sketch, "E208.MirrorCS", {"start": v(2249.42, -114.3) * mm, "end": v(2249.42, -236.98) * mm});
            skLineSegment(sketch, "E209.MirrorCS", {"start": v(2474.98, -114.3) * mm, "end": v(2474.98, -236.98) * mm});
            skLineSegment(sketch, "E210.MirrorCS", {"start": v(2235.2, -114.3) * mm, "end": v(2235.2, -368.3) * mm});
            skLineSegment(sketch, "E211.MirrorCS", {"start": v(2489.2, -114.3) * mm, "end": v(2489.2, -368.3) * mm});
            skSolve(sketch);
        }
        {
            var Q0;
            Q0=qSketchRegion(id+"F13",true);
            extrude(context, id + "F14", {"entities" : qUnion([Q0]), "depth" : 198.37 * mm});
        }
        {
            var Q0;
            Q0=makeQuery(id+"F12.opExtrude","SWEPT_FACE",FACE,{"disambiguationData":[OSD([sQuery(id+"F11.wireOp",EDGE,"E169.top")])]});
            var sketch = newSketch(context, id + "F15", { "sketchPlane" : qUnion([Q0])});
            skLineSegment(sketch, "E212.0", {"start": v(-1615.4, -241.3) * mm, "end": v(2831.5, -241.3) * mm, "construction": true});
            skLineSegment(sketch, "E213.0", {"start": v(0, -413.23) * mm, "end": v(0, 639.03) * mm, "construction": true});
            skPoint(sketch, "E214.orphan", {"position": v(-1320.8, -241.3) * mm});
            skLineSegment(sketch, "E215.0", {"start": v(-1168.4, -689.85) * mm, "end": v(-1168.4, 639.03) * mm, "construction": true});
            skLineSegment(sketch, "E216.0", {"start": v(-1130.3, -355.6) * mm, "end": v(-1130.3, -127) * mm});
            skLineSegment(sketch, "E217.0", {"start": v(-1206.5, -127) * mm, "end": v(-1130.3, -127) * mm});
            skLineSegment(sketch, "E218.0", {"start": v(-1615.4, -171.45) * mm, "end": v(2831.5, -171.45) * mm, "construction": true});
            skLineSegment(sketch, "E219.MirrorCS", {"start": v(-1206.5, -355.6) * mm, "end": v(-1130.3, -355.6) * mm});
            skLineSegment(sketch, "E220.MirrorCS", {"start": v(-1206.5, -355.6) * mm, "end": v(-1206.5, -127) * mm});
            skPoint(sketch, "E221.orphan", {"position": v(-1130.3, 639.03) * mm});
            skPoint(sketch, "E222.orphan", {"position": v(-1206.5, 639.03) * mm});
            skPoint(sketch, "E223.orphan", {"position": v(-1615.4, -127) * mm});
            skPoint(sketch, "E224.orphan", {"position": v(-1615.4, -355.6) * mm});
            skPoint(sketch, "E225.orphan", {"position": v(-1206.5, -689.85) * mm});
            skPoint(sketch, "E226.orphan", {"position": v(-1130.3, -689.85) * mm});
            skCircle(sketch, "E227", {"center": v(-1168.4, -171.45) * mm, "radius": 11.11 * mm});
            skCircle(sketch, "E228.MirrorC", {"center": v(-1168.4, -311.15) * mm, "radius": 11.11 * mm});
            skLineSegment(sketch, "E229.1.0.0", {"start": v(1130.3, -355.6) * mm, "end": v(1130.3, -127) * mm});
            skLineSegment(sketch, "E229.1.0.1", {"start": v(1130.3, -355.6) * mm, "end": v(1206.5, -355.6) * mm});
            skLineSegment(sketch, "E229.1.0.2", {"start": v(1130.3, -127) * mm, "end": v(1206.5, -127) * mm});
            skLineSegment(sketch, "E229.1.0.3", {"start": v(1206.5, -355.6) * mm, "end": v(1206.5, -127) * mm});
            skCircle(sketch, "E229.1.0.4", {"center": v(1168.4, -171.45) * mm, "radius": 11.11 * mm});
            skCircle(sketch, "E229.1.0.5", {"center": v(1168.4, -311.15) * mm, "radius": 11.11 * mm});
            skLineSegment(sketch, "E229.direction1", {"start": v(-1206.5, -355.6) * mm, "end": v(1130.3, -355.6) * mm, "construction": true});
            skLineSegment(sketch, "E230.1.0.1", {"start": v(2578.1, -355.6) * mm, "end": v(2578.1, -127) * mm});
            skLineSegment(sketch, "E230.1.0.2", {"start": v(2654.3, -355.6) * mm, "end": v(2654.3, -127) * mm});
            skCircle(sketch, "E230.1.0.3", {"center": v(2616.2, -311.15) * mm, "radius": 11.11 * mm});
            skCircle(sketch, "E230.1.0.4", {"center": v(2616.2, -171.45) * mm, "radius": 11.11 * mm});
            skLineSegment(sketch, "E230.1.0.5", {"start": v(2578.1, -355.6) * mm, "end": v(2654.3, -355.6) * mm});
            skLineSegment(sketch, "E230.1.0.6", {"start": v(2578.1, -127) * mm, "end": v(2654.3, -127) * mm});
            skLineSegment(sketch, "E230.direction1", {"start": v(1320.8, -241.3) * mm, "end": v(2768.6, -241.3) * mm, "construction": true});
            skSolve(sketch);
        }
        {
            var Q0;
            Q0=qSketchRegion(id+"F15",true);
            extrude(context, id + "F16", {"entities" : qUnion([Q0]), "operationType" : NewBodyOperationType.ADD, "depth" : 19.05 * mm});
        }
        {
            var Q0;
            Q0=makeQuery(id+"F12.opExtrude","SWEPT_FACE",FACE,{"disambiguationData":[OSD([sQuery(id+"F11.wireOp",EDGE,"E173.MirrorCS")])]});
            var sketch = newSketch(context, id + "F17", { "sketchPlane" : qUnion([Q0])});
            skLineSegment(sketch, "E231", {"start": v(0, -262.73) * mm, "end": v(0, 1224.7) * mm, "construction": true});
            skLineSegment(sketch, "E232.0", {"start": v(-1320.8, 0) * mm, "end": v(1320.8, 0) * mm, "construction": true});
            skLineSegment(sketch, "E233.0", {"start": v(-1320.8, 231.9) * mm, "end": v(1320.8, 231.9) * mm, "construction": true});
            skLineSegment(sketch, "E234.0", {"start": v(-1187.45, -262.73) * mm, "end": v(-1187.45, 1224.7) * mm, "construction": true});
            skLineSegment(sketch, "E235.0", {"start": v(-1320.8, 333.5) * mm, "end": v(1320.8, 333.5) * mm, "construction": true});
            skLineSegment(sketch, "E236.bottom", {"start": v(-1289.05, 435.1) * mm, "end": v(-1085.85, 435.1) * mm});
            skLineSegment(sketch, "E236.top", {"start": v(-1289.05, 231.9) * mm, "end": v(-1085.85, 231.9) * mm});
            skLineSegment(sketch, "E236.left", {"start": v(-1289.05, 435.1) * mm, "end": v(-1289.05, 424.05) * mm});
            skLineSegment(sketch, "E236.right", {"start": v(-1085.85, 435.1) * mm, "end": v(-1085.85, 424.05) * mm});
            skPoint(sketch, "E236.middle", {"position": v(-1187.45, 333.5) * mm});
            skLineSegment(sketch, "E237.0", {"start": v(-1289.05, 424.05) * mm, "end": v(-1197.36, 424.05) * mm});
            skLineSegment(sketch, "E238.MirrorCS", {"start": v(-1289.05, 242.95) * mm, "end": v(-1197.36, 242.95) * mm});
            skLineSegment(sketch, "E239.0", {"start": v(-1183.9, 249.3) * mm, "end": v(-1183.9, 417.7) * mm});
            skLineSegment(sketch, "E240.MirrorCS", {"start": v(-1191, 249.3) * mm, "end": v(-1191, 417.7) * mm});
            skLineSegment(sketch, "E241", {"start": v(-1177.54, 424.05) * mm, "end": v(-1085.85, 424.05) * mm});
            skLineSegment(sketch, "E242", {"start": v(-1177.54, 242.95) * mm, "end": v(-1085.85, 242.95) * mm});
            skPoint(sketch, "E243.newPointB", {"position": v(-1191, 1224.7) * mm});
            skArc(sketch, "E243.filletArc", {"start": v(-1191, 417.7) * mm, "mid": v(-1192.87, 422.2) * mm, "end": v(-1197.36, 424.05) * mm});
            skPoint(sketch, "E244.newPointA", {"position": v(-1191, -262.73) * mm});
            skArc(sketch, "E244.filletArc", {"start": v(-1197.36, 242.95) * mm, "mid": v(-1192.87, 244.81) * mm, "end": v(-1191, 249.3) * mm});
            skPoint(sketch, "E245.newPointA", {"position": v(-1183.9, -262.73) * mm});
            skArc(sketch, "E245.filletArc", {"start": v(-1183.9, 249.3) * mm, "mid": v(-1182.03, 244.81) * mm, "end": v(-1177.54, 242.95) * mm});
            skPoint(sketch, "E246.newPointB", {"position": v(-1183.9, 1224.7) * mm});
            skArc(sketch, "E246.filletArc", {"start": v(-1177.54, 424.05) * mm, "mid": v(-1182.03, 422.2) * mm, "end": v(-1183.9, 417.7) * mm});
            skLineSegment(sketch, "E247.trimOffspring", {"start": v(-1289.05, 242.95) * mm, "end": v(-1289.05, 231.9) * mm});
            skLineSegment(sketch, "E248.trimOffspring", {"start": v(-1085.85, 242.95) * mm, "end": v(-1085.85, 231.9) * mm});
            skArc(sketch, "E249.MirrorCS", {"start": v(1177.54, 424.05) * mm, "mid": v(1182.03, 422.2) * mm, "end": v(1183.9, 417.7) * mm});
            skArc(sketch, "E250.MirrorCS", {"start": v(1183.9, 249.3) * mm, "mid": v(1182.03, 244.81) * mm, "end": v(1177.54, 242.95) * mm});
            skArc(sketch, "E251.MirrorCS", {"start": v(1197.36, 242.95) * mm, "mid": v(1192.87, 244.81) * mm, "end": v(1191, 249.3) * mm});
            skArc(sketch, "E252.MirrorCS", {"start": v(1191, 417.7) * mm, "mid": v(1192.87, 422.2) * mm, "end": v(1197.36, 424.05) * mm});
            skLineSegment(sketch, "E253.MirrorCS", {"start": v(1085.85, 242.95) * mm, "end": v(1085.85, 231.9) * mm});
            skLineSegment(sketch, "E254.MirrorCS", {"start": v(1183.9, 249.3) * mm, "end": v(1183.9, 417.7) * mm});
            skLineSegment(sketch, "E255.MirrorCS", {"start": v(1289.05, 242.95) * mm, "end": v(1289.05, 231.9) * mm});
            skLineSegment(sketch, "E256.MirrorCS", {"start": v(1085.85, 435.1) * mm, "end": v(1085.85, 424.05) * mm});
            skLineSegment(sketch, "E257.MirrorCS", {"start": v(1289.05, 435.1) * mm, "end": v(1289.05, 424.05) * mm});
            skLineSegment(sketch, "E258.MirrorCS", {"start": v(1289.05, 242.95) * mm, "end": v(1197.36, 242.95) * mm});
            skLineSegment(sketch, "E259.MirrorCS", {"start": v(1289.05, 424.05) * mm, "end": v(1197.36, 424.05) * mm});
            skLineSegment(sketch, "E260.MirrorCS", {"start": v(1289.05, 435.1) * mm, "end": v(1085.85, 435.1) * mm});
            skLineSegment(sketch, "E261.MirrorCS", {"start": v(1177.54, 424.05) * mm, "end": v(1085.85, 424.05) * mm});
            skLineSegment(sketch, "E262.MirrorCS", {"start": v(1289.05, 231.9) * mm, "end": v(1085.85, 231.9) * mm});
            skLineSegment(sketch, "E263.MirrorCS", {"start": v(1177.54, 242.95) * mm, "end": v(1085.85, 242.95) * mm});
            skLineSegment(sketch, "E264.MirrorCS", {"start": v(1191, 249.3) * mm, "end": v(1191, 417.7) * mm});
            skPoint(sketch, "E265.MirrorP", {"position": v(1187.45, 333.5) * mm});
            skSolve(sketch);
        }
        {
            var Q0;
            Q0=qSketchRegion(id+"F17",true);
            extrude(context, id + "F18", {"entities" : qUnion([Q0]), "depth" : 401.57 * mm});
        }
        {
            var Q0;
            Q0=makeQuery(id+"F18.opExtrude","SWEPT_FACE",FACE,{"disambiguationData":[OSD([sQuery(id+"F17.wireOp",EDGE,"E236.bottom")])]});
            var sketch = newSketch(context, id + "F19", { "sketchPlane" : qUnion([Q0])});
            skLineSegment(sketch, "E266.bottom", {"start": v(-1289.05, -649.22) * mm, "end": v(-1278, -649.22) * mm});
            skLineSegment(sketch, "E266.top", {"start": v(-1289.05, -446.02) * mm, "end": v(-1278, -446.02) * mm});
            skLineSegment(sketch, "E266.left", {"start": v(-1289.05, -649.22) * mm, "end": v(-1289.05, -446.02) * mm});
            skLineSegment(sketch, "E266.right", {"start": v(-1085.85, -649.22) * mm, "end": v(-1085.85, -446.02) * mm});
            skLineSegment(sketch, "E267", {"start": v(-1187.45, -446.02) * mm, "end": v(-1187.45, -700.9) * mm, "construction": true});
            skLineSegment(sketch, "E268", {"start": v(-1289.05, -547.62) * mm, "end": v(-1023.84, -547.62) * mm, "construction": true});
            skLineSegment(sketch, "E269.0", {"start": v(-1278, -649.22) * mm, "end": v(-1278, -557.53) * mm});
            skLineSegment(sketch, "E270.MirrorCS", {"start": v(-1096.9, -649.22) * mm, "end": v(-1096.9, -557.53) * mm});
            skLineSegment(sketch, "E271.0", {"start": v(-1271.65, -551.18) * mm, "end": v(-1103.25, -551.18) * mm});
            skLineSegment(sketch, "E272.MirrorCS", {"start": v(-1271.65, -544.07) * mm, "end": v(-1103.25, -544.07) * mm});
            skPoint(sketch, "E273.orphan", {"position": v(-1023.84, -551.18) * mm});
            skPoint(sketch, "E274.orphan", {"position": v(-1023.84, -544.07) * mm});
            skLineSegment(sketch, "E275.trimOffspring", {"start": v(-1096.9, -537.72) * mm, "end": v(-1096.9, -446.02) * mm});
            skPoint(sketch, "E276.orphan", {"position": v(-1289.05, -544.07) * mm});
            skLineSegment(sketch, "E277.trimOffspring", {"start": v(-1278, -537.72) * mm, "end": v(-1278, -446.02) * mm});
            skPoint(sketch, "E278.orphan", {"position": v(-1289.05, -551.18) * mm});
            skLineSegment(sketch, "E279.trimOffspring", {"start": v(-1096.9, -446.02) * mm, "end": v(-1085.85, -446.02) * mm});
            skLineSegment(sketch, "E280.trimOffspring", {"start": v(-1096.9, -649.22) * mm, "end": v(-1085.85, -649.22) * mm});
            skPoint(sketch, "E281.visualSharp", {"position": v(-1278, -544.07) * mm});
            skArc(sketch, "E281.filletArc", {"start": v(-1278, -537.72) * mm, "mid": v(-1276.14, -542.2) * mm, "end": v(-1271.65, -544.07) * mm});
            skPoint(sketch, "E282.visualSharp", {"position": v(-1278, -551.18) * mm});
            skArc(sketch, "E282.filletArc", {"start": v(-1271.65, -551.18) * mm, "mid": v(-1276.14, -553.04) * mm, "end": v(-1278, -557.53) * mm});
            skPoint(sketch, "E283.visualSharp", {"position": v(-1096.9, -551.18) * mm});
            skArc(sketch, "E283.filletArc", {"start": v(-1096.9, -557.53) * mm, "mid": v(-1098.76, -553.04) * mm, "end": v(-1103.25, -551.18) * mm});
            skPoint(sketch, "E284.visualSharp", {"position": v(-1096.9, -544.07) * mm});
            skArc(sketch, "E284.filletArc", {"start": v(-1103.25, -544.07) * mm, "mid": v(-1098.76, -542.2) * mm, "end": v(-1096.9, -537.72) * mm});
            skArc(sketch, "E285.MirrorCS", {"start": v(1271.65, -551.18) * mm, "mid": v(1276.14, -553.04) * mm, "end": v(1278, -557.53) * mm});
            skArc(sketch, "E286.MirrorCS", {"start": v(1278, -537.72) * mm, "mid": v(1276.14, -542.2) * mm, "end": v(1271.65, -544.07) * mm});
            skArc(sketch, "E287.MirrorCS", {"start": v(1096.9, -557.53) * mm, "mid": v(1098.76, -553.04) * mm, "end": v(1103.25, -551.18) * mm});
            skArc(sketch, "E288.MirrorCS", {"start": v(1103.25, -544.07) * mm, "mid": v(1098.76, -542.2) * mm, "end": v(1096.9, -537.72) * mm});
            skLineSegment(sketch, "E289.MirrorCS", {"start": v(1289.05, -547.62) * mm, "end": v(1023.84, -547.62) * mm, "construction": true});
            skLineSegment(sketch, "E290.MirrorCS", {"start": v(1096.9, -649.22) * mm, "end": v(1085.85, -649.22) * mm});
            skLineSegment(sketch, "E291.MirrorCS", {"start": v(1289.05, -649.22) * mm, "end": v(1278, -649.22) * mm});
            skLineSegment(sketch, "E292.MirrorCS", {"start": v(1289.05, -446.02) * mm, "end": v(1278, -446.02) * mm});
            skPoint(sketch, "E293.MirrorP", {"position": v(1096.9, -551.18) * mm});
            skLineSegment(sketch, "E294.MirrorCS", {"start": v(1096.9, -446.02) * mm, "end": v(1085.85, -446.02) * mm});
            skPoint(sketch, "E295.MirrorP", {"position": v(1289.05, -544.07) * mm});
            skPoint(sketch, "E296.MirrorP", {"position": v(1278, -551.18) * mm});
            skLineSegment(sketch, "E297.MirrorCS", {"start": v(1271.65, -551.18) * mm, "end": v(1103.25, -551.18) * mm});
            skLineSegment(sketch, "E298.MirrorCS", {"start": v(1289.05, -649.22) * mm, "end": v(1289.05, -446.02) * mm});
            skPoint(sketch, "E299.MirrorP", {"position": v(1289.05, -551.18) * mm});
            skLineSegment(sketch, "E300.MirrorCS", {"start": v(1085.85, -649.22) * mm, "end": v(1085.85, -446.02) * mm});
            skPoint(sketch, "E301.MirrorP", {"position": v(1278, -544.07) * mm});
            skLineSegment(sketch, "E302.MirrorCS", {"start": v(1096.9, -649.22) * mm, "end": v(1096.9, -557.53) * mm});
            skLineSegment(sketch, "E303.MirrorCS", {"start": v(1278, -537.72) * mm, "end": v(1278, -446.02) * mm});
            skLineSegment(sketch, "E304.MirrorCS", {"start": v(1278, -649.22) * mm, "end": v(1278, -557.53) * mm});
            skLineSegment(sketch, "E305.MirrorCS", {"start": v(1271.65, -544.07) * mm, "end": v(1103.25, -544.07) * mm});
            skPoint(sketch, "E306.MirrorP", {"position": v(1096.9, -544.07) * mm});
            skPoint(sketch, "E307.MirrorP", {"position": v(1023.84, -544.07) * mm});
            skLineSegment(sketch, "E308.MirrorCS", {"start": v(1096.9, -537.72) * mm, "end": v(1096.9, -446.02) * mm});
            skLineSegment(sketch, "E309.MirrorCS", {"start": v(1187.45, -446.02) * mm, "end": v(1187.45, -700.9) * mm, "construction": true});
            skPoint(sketch, "E310.MirrorP", {"position": v(1023.84, -551.18) * mm});
            skSolve(sketch);
        }
        {
            var Q0;
            Q0=qSketchRegion(id+"F19",true);
            extrude(context, id + "F20", {"entities" : qUnion([Q0]), "depth" : 292.1 * mm});
        }
        {
            var Q0;
            Q0=makeQuery(id+"F20.opExtrude","CAP_FACE",FACE,{"disambiguationData":[OSD([sQuery(id+"F19.wireOp",EDGE,"E266.bottom"),sQuery(id+"F19.wireOp",EDGE,"E266.top"),sQuery(id+"F19.wireOp",EDGE,"E266.left"),sQuery(id+"F19.wireOp",EDGE,"E266.right"),sQuery(id+"F19.wireOp",EDGE,"E269.0"),sQuery(id+"F19.wireOp",EDGE,"E270.MirrorCS"),sQuery(id+"F19.wireOp",EDGE,"E271.0"),sQuery(id+"F19.wireOp",EDGE,"E272.MirrorCS"),sQuery(id+"F19.wireOp",EDGE,"E275.trimOffspring"),sQuery(id+"F19.wireOp",EDGE,"E277.trimOffspring"),sQuery(id+"F19.wireOp",EDGE,"E279.trimOffspring"),sQuery(id+"F19.wireOp",EDGE,"E280.trimOffspring"),sQuery(id+"F19.wireOp",EDGE,"E281.filletArc"),sQuery(id+"F19.wireOp",EDGE,"E282.filletArc"),sQuery(id+"F19.wireOp",EDGE,"E283.filletArc"),sQuery(id+"F19.wireOp",EDGE,"E284.filletArc")])],"isStart":false});
            var sketch = newSketch(context, id + "F21", { "sketchPlane" : qUnion([Q0])});
            skLineSegment(sketch, "E311.0", {"start": v(-1289.05, -649.22) * mm, "end": v(-1289.05, -446.02) * mm, "construction": true});
            skLineSegment(sketch, "E312.0", {"start": v(-1085.85, -649.22) * mm, "end": v(-1085.85, -446.02) * mm, "construction": true});
            skLineSegment(sketch, "E313", {"start": v(-1289.05, -547.62) * mm, "end": v(-1085.85, -547.62) * mm, "construction": true});
            skLineSegment(sketch, "E314.bottom", {"start": v(-1301.75, -433.32) * mm, "end": v(-1073.15, -433.32) * mm});
            skLineSegment(sketch, "E314.top", {"start": v(-1301.75, -661.92) * mm, "end": v(-1073.15, -661.92) * mm});
            skLineSegment(sketch, "E314.left", {"start": v(-1301.75, -433.32) * mm, "end": v(-1301.75, -661.92) * mm});
            skLineSegment(sketch, "E314.right", {"start": v(-1073.15, -433.32) * mm, "end": v(-1073.15, -661.92) * mm});
            skPoint(sketch, "E314.middle", {"position": v(-1187.45, -547.62) * mm});
            skLineSegment(sketch, "E315", {"start": v(-1187.45, -433.32) * mm, "end": v(-1187.45, -661.92) * mm, "construction": true});
            skLineSegment(sketch, "E316.0", {"start": v(-1289.05, -477.77) * mm, "end": v(-1085.85, -477.77) * mm, "construction": true});
            skCircle(sketch, "E317", {"center": v(-1187.45, -477.77) * mm, "radius": 11.11 * mm});
            skCircle(sketch, "E318.MirrorC", {"center": v(-1187.45, -617.47) * mm, "radius": 11.11 * mm});
            skCircle(sketch, "E319.MirrorC", {"center": v(1187.45, -617.47) * mm, "radius": 11.11 * mm});
            skCircle(sketch, "E320.MirrorC", {"center": v(1187.45, -477.77) * mm, "radius": 11.11 * mm});
            skLineSegment(sketch, "E321.MirrorCS", {"start": v(1289.05, -477.77) * mm, "end": v(1085.85, -477.77) * mm, "construction": true});
            skLineSegment(sketch, "E322.MirrorCS", {"start": v(1289.05, -547.62) * mm, "end": v(1085.85, -547.62) * mm, "construction": true});
            skLineSegment(sketch, "E323.MirrorCS", {"start": v(1289.05, -649.22) * mm, "end": v(1289.05, -446.02) * mm, "construction": true});
            skLineSegment(sketch, "E324.MirrorCS", {"start": v(1187.45, -433.32) * mm, "end": v(1187.45, -661.92) * mm, "construction": true});
            skPoint(sketch, "E325.MirrorP", {"position": v(1187.45, -547.62) * mm});
            skLineSegment(sketch, "E326.MirrorCS", {"start": v(1073.15, -433.32) * mm, "end": v(1073.15, -661.92) * mm});
            skLineSegment(sketch, "E327.MirrorCS", {"start": v(1301.75, -661.92) * mm, "end": v(1073.15, -661.92) * mm});
            skLineSegment(sketch, "E328.MirrorCS", {"start": v(1301.75, -433.32) * mm, "end": v(1073.15, -433.32) * mm});
            skLineSegment(sketch, "E329.MirrorCS", {"start": v(1085.85, -649.22) * mm, "end": v(1085.85, -446.02) * mm, "construction": true});
            skLineSegment(sketch, "E330.MirrorCS", {"start": v(1301.75, -433.32) * mm, "end": v(1301.75, -661.92) * mm});
            skSolve(sketch);
        }
        {
            var Q0;
            Q0=qSketchRegion(id+"F21",true);
            extrude(context, id + "F22", {"entities" : qUnion([Q0]), "depth" : 19.05 * mm});
        }
        {
            var Q0;
            Q0=makeQuery(id+"F20.opExtrude","SWEPT_FACE",FACE,{"disambiguationData":[OSD([sQuery(id+"F19.wireOp",EDGE,"E266.right")])]});
            var sketch = newSketch(context, id + "F23", { "sketchPlane" : qUnion([Q0])});
            skLineSegment(sketch, "E331.0.0", {"start": v(-649.22, 435.1) * mm, "end": v(-446.02, 435.1) * mm, "construction": true});
            skLineSegment(sketch, "E331.0.1", {"start": v(-446.02, 435.1) * mm, "end": v(-446.02, 727.2) * mm, "construction": true});
            skLineSegment(sketch, "E331.0.2", {"start": v(-446.02, 727.2) * mm, "end": v(-649.22, 727.2) * mm, "construction": true});
            skLineSegment(sketch, "E331.0.3", {"start": v(-649.22, 727.2) * mm, "end": v(-649.22, 435.1) * mm, "construction": true});
            skLineSegment(sketch, "E332.0", {"start": v(-446.02, 574.8) * mm, "end": v(-649.22, 574.8) * mm, "construction": true});
            skLineSegment(sketch, "E333", {"start": v(-547.62, 574.8) * mm, "end": v(-547.62, 602) * mm, "construction": true});
            skCircle(sketch, "E334", {"center": v(-547.62, 574.8) * mm, "radius": 44.45 * mm});
            skCircle(sketch, "E335.0", {"center": v(-547.62, 574.8) * mm, "radius": 38.96 * mm});
            skSolve(sketch);
        }
        {
            var Q0;
            Q0=qSketchRegion(id+"F23",true);
            extrude(context, id + "F24", {"entities" : qUnion([Q0]), "depth" : 2171.7 * mm});
        }
        {
            var Q0;
            Q0=makeQuery(id+"F16.opExtrude","CAP_FACE",FACE,{"disambiguationData":[OSD([sQuery(id+"F15.wireOp",EDGE,"E229.1.0.0"),sQuery(id+"F15.wireOp",EDGE,"E229.1.0.1"),sQuery(id+"F15.wireOp",EDGE,"E229.1.0.2"),sQuery(id+"F15.wireOp",EDGE,"E229.1.0.3"),sQuery(id+"F15.wireOp",EDGE,"E229.1.0.4"),sQuery(id+"F15.wireOp",EDGE,"E229.1.0.5")])],"isStart":false});
            var sketch = newSketch(context, id + "F25", { "sketchPlane" : qUnion([Q0])});
            skLineSegment(sketch, "E336.0.0", {"start": v(1130.3, -127) * mm, "end": v(1130.3, -355.6) * mm});
            skLineSegment(sketch, "E336.0.1", {"start": v(1130.3, -355.6) * mm, "end": v(1206.5, -355.6) * mm});
            skLineSegment(sketch, "E336.0.2", {"start": v(1206.5, -355.6) * mm, "end": v(1206.5, -127) * mm});
            skLineSegment(sketch, "E336.0.3", {"start": v(1206.5, -127) * mm, "end": v(1130.3, -127) * mm});
            skCircle(sketch, "E337.0", {"center": v(1168.4, -311.15) * mm, "radius": 11.11 * mm});
            skCircle(sketch, "E338.0", {"center": v(1168.4, -171.45) * mm, "radius": 11.11 * mm});
            skLineSegment(sketch, "E339.0.0", {"start": v(2578.1, -127) * mm, "end": v(2578.1, -355.6) * mm});
            skLineSegment(sketch, "E339.0.1", {"start": v(2578.1, -355.6) * mm, "end": v(2654.3, -355.6) * mm});
            skLineSegment(sketch, "E339.0.2", {"start": v(2654.3, -355.6) * mm, "end": v(2654.3, -127) * mm});
            skLineSegment(sketch, "E339.0.3", {"start": v(2654.3, -127) * mm, "end": v(2578.1, -127) * mm});
            skCircle(sketch, "E340.0", {"center": v(2616.2, -171.45) * mm, "radius": 11.11 * mm});
            skCircle(sketch, "E341.0", {"center": v(2616.2, -311.15) * mm, "radius": 11.11 * mm});
            skSolve(sketch);
        }
        {
            var Q0;
            Q0=qSketchRegion(id+"F25",true);
            extrude(context, id + "F26", {"entities" : qUnion([Q0]), "depth" : 19 * mm});
        }
        {
            var Q0;
            {var subQ7=sQuery(id+"F11.wireOp",EDGE,"E174.trimOffspring");var subQ14=sQuery(id+"F11.wireOp",EDGE,"E169.top");Q0=makeQuery(id+"F16.boolean.opBoolean","SPLIT",FACE,{"disambiguationData":[TD([makeQuery(id+"F12.opExtrude","SWEPT_FACE",FACE,{"disambiguationData":[OSD([subQ7])]})])],"derivedFrom":makeQuery(id+"F12.opExtrude","SWEPT_FACE",FACE,{"disambiguationData":[OSD([subQ14])]})});}
            cPlane(context, id + "F27", {"entities" : qUnion([Q0]), "cplaneType" : CPlaneType.OFFSET, "offset" : 108 * mm, "width" : 150 * mm, "height" : 150 * mm});
        }
        {
            var Q0;
            Q0=qCreatedBy(id+"F27.planeOp",FACE);
            var sketch = newSketch(context, id + "F28", { "sketchPlane" : qUnion([Q0])});
            skLineSegment(sketch, "E342.0", {"start": v(2692.4, -1524.13) * mm, "end": v(2692.4, 788.61) * mm, "construction": true});
            skPoint(sketch, "E343.orphan", {"position": v(2692.4, -114.3) * mm});
            skPoint(sketch, "E344.orphan", {"position": v(2692.4, -368.3) * mm});
            skLineSegment(sketch, "E345.0", {"start": v(948.9, -1524.13) * mm, "end": v(948.9, 788.61) * mm, "construction": true});
            skLineSegment(sketch, "E346.0", {"start": v(1023.9, -1524.13) * mm, "end": v(1023.9, 788.61) * mm, "construction": true});
            skLineSegment(sketch, "E347.0", {"start": v(-1460.5, -368.3) * mm, "end": v(-1460.5, -114.3) * mm, "construction": true});
            skLineSegment(sketch, "E348", {"start": v(-1460.5, -241.3) * mm, "end": v(2900.96, -241.3) * mm, "construction": true});
            skPoint(sketch, "E348.endSnap0", {"position": v(-1460.5, -241.3) * mm});
            skLineSegment(sketch, "E349.bottom", {"start": v(948.9, -51.3) * mm, "end": v(1098.9, -51.3) * mm});
            skLineSegment(sketch, "E349.top", {"start": v(948.9, -431.3) * mm, "end": v(1098.9, -431.3) * mm});
            skLineSegment(sketch, "E349.left", {"start": v(948.9, -51.3) * mm, "end": v(948.9, -431.3) * mm});
            skLineSegment(sketch, "E349.right", {"start": v(1098.9, -51.3) * mm, "end": v(1098.9, -431.3) * mm});
            skPoint(sketch, "E349.middle", {"position": v(1023.9, -241.3) * mm});
            skLineSegment(sketch, "E350.0", {"start": v(-1460.5, -86.3) * mm, "end": v(2900.96, -86.3) * mm, "construction": true});
            skCircle(sketch, "E351", {"center": v(1023.9, -86.3) * mm, "radius": 7.25 * mm});
            skCircle(sketch, "E352.MirrorC", {"center": v(1023.9, -396.3) * mm, "radius": 7.25 * mm});
            skPoint(sketch, "E353.1.0.0", {"position": v(1698.9, -241.3) * mm});
            skLineSegment(sketch, "E353.1.0.1", {"start": v(1773.9, -51.3) * mm, "end": v(1773.9, -431.3) * mm});
            skLineSegment(sketch, "E353.1.0.2", {"start": v(1623.9, -51.3) * mm, "end": v(1773.9, -51.3) * mm});
            skLineSegment(sketch, "E353.1.0.3", {"start": v(1623.9, -431.3) * mm, "end": v(1773.9, -431.3) * mm});
            skLineSegment(sketch, "E353.1.0.4", {"start": v(1623.9, -51.3) * mm, "end": v(1623.9, -431.3) * mm});
            skCircle(sketch, "E353.1.0.5", {"center": v(1698.9, -396.3) * mm, "radius": 7.25 * mm});
            skCircle(sketch, "E353.1.0.6", {"center": v(1698.9, -86.3) * mm, "radius": 7.25 * mm});
            skPoint(sketch, "E353.2.0.0", {"position": v(2373.9, -241.3) * mm});
            skLineSegment(sketch, "E353.2.0.1", {"start": v(2448.9, -51.3) * mm, "end": v(2448.9, -431.3) * mm});
            skLineSegment(sketch, "E353.2.0.2", {"start": v(2298.9, -51.3) * mm, "end": v(2448.9, -51.3) * mm});
            skLineSegment(sketch, "E353.2.0.3", {"start": v(2298.9, -431.3) * mm, "end": v(2448.9, -431.3) * mm});
            skLineSegment(sketch, "E353.2.0.4", {"start": v(2298.9, -51.3) * mm, "end": v(2298.9, -431.3) * mm});
            skCircle(sketch, "E353.2.0.5", {"center": v(2373.9, -396.3) * mm, "radius": 7.25 * mm});
            skCircle(sketch, "E353.2.0.6", {"center": v(2373.9, -86.3) * mm, "radius": 7.25 * mm});
            skLineSegment(sketch, "E353.direction1", {"start": v(1023.9, -241.3) * mm, "end": v(1698.9, -241.3) * mm, "construction": true});
            skPoint(sketch, "E354.0.3.0", {"position": v(3048.9, -241.3) * mm});
            skLineSegment(sketch, "E354.1.3.0", {"start": v(3123.9, -51.3) * mm, "end": v(3123.9, -431.3) * mm});
            skLineSegment(sketch, "E354.4.3.0", {"start": v(2973.9, -51.3) * mm, "end": v(3123.9, -51.3) * mm});
            skLineSegment(sketch, "E354.7.3.0", {"start": v(2973.9, -431.3) * mm, "end": v(3123.9, -431.3) * mm});
            skLineSegment(sketch, "E354.10.3.0", {"start": v(2973.9, -51.3) * mm, "end": v(2973.9, -431.3) * mm});
            skCircle(sketch, "E354.13.3.0", {"center": v(3048.9, -396.3) * mm, "radius": 7.25 * mm});
            skCircle(sketch, "E354.15.3.0", {"center": v(3048.9, -86.3) * mm, "radius": 7.25 * mm});
            skPoint(sketch, "E354.0.4.0", {"position": v(3723.9, -241.3) * mm});
            skLineSegment(sketch, "E354.1.4.0", {"start": v(3798.9, -51.3) * mm, "end": v(3798.9, -431.3) * mm});
            skLineSegment(sketch, "E354.4.4.0", {"start": v(3648.9, -51.3) * mm, "end": v(3798.9, -51.3) * mm});
            skLineSegment(sketch, "E354.7.4.0", {"start": v(3648.9, -431.3) * mm, "end": v(3798.9, -431.3) * mm});
            skLineSegment(sketch, "E354.10.4.0", {"start": v(3648.9, -51.3) * mm, "end": v(3648.9, -431.3) * mm});
            skCircle(sketch, "E354.13.4.0", {"center": v(3723.9, -396.3) * mm, "radius": 7.25 * mm});
            skCircle(sketch, "E354.15.4.0", {"center": v(3723.9, -86.3) * mm, "radius": 7.25 * mm});
            skSolve(sketch);
        }
        {
            var Q0;
            Q0=qSketchRegion(id+"F28",true);
            extrude(context, id + "F29", {"entities" : qUnion([Q0]), "oppositeDirection" : true, "depth" : 19 * mm});
        }
        {
            var Q0;
            Q0=makeQuery(id+"F26.opExtrude","SWEPT_FACE",FACE,{"disambiguationData":[OSD([sQuery(id+"F25.wireOp",EDGE,"E336.0.1")])]});
            var Q1;
            Q1=makeQuery(id+"F26.opExtrude","SWEPT_FACE",FACE,{"disambiguationData":[OSD([sQuery(id+"F25.wireOp",EDGE,"E336.0.3")])]});
            cPlane(context, id + "F30", {"entities" : qUnion([Q0, Q1]), "cplaneType" : CPlaneType.MID_PLANE, "offset" : 150 * mm, "width" : 150 * mm, "height" : 150 * mm});
        }
        {
            var Q0;
            Q0=qCreatedBy(id+"F10.planeOp",FACE);
            var sketch = newSketch(context, id + "F31", { "sketchPlane" : qUnion([Q0])});
            skLineSegment(sketch, "E355.0.0", {"start": v(-368.3, 231.65) * mm, "end": v(-368.3, 217.42) * mm, "construction": true});
            skLineSegment(sketch, "E355.0.1", {"start": v(-368.3, 217.42) * mm, "end": v(-114.3, 217.42) * mm, "construction": true});
            skLineSegment(sketch, "E355.0.2", {"start": v(-114.3, 217.42) * mm, "end": v(-114.3, 231.65) * mm, "construction": true});
            skLineSegment(sketch, "E355.0.3", {"start": v(-114.3, 231.65) * mm, "end": v(-228.6, 231.65) * mm, "construction": true});
            skArc(sketch, "E355.0.4", {"start": v(-228.6, 231.65) * mm, "mid": v(-233.1, 233.5) * mm, "end": v(-234.95, 238) * mm, "construction": true});
            skLineSegment(sketch, "E355.0.5", {"start": v(-234.95, 238) * mm, "end": v(-234.95, 450.85) * mm, "construction": true});
            skArc(sketch, "E355.0.6", {"start": v(-234.95, 450.85) * mm, "mid": v(-233.1, 455.34) * mm, "end": v(-228.6, 457.2) * mm, "construction": true});
            skLineSegment(sketch, "E355.0.7", {"start": v(-228.6, 457.2) * mm, "end": v(-114.3, 457.2) * mm, "construction": true});
            skLineSegment(sketch, "E355.0.8", {"start": v(-114.3, 457.2) * mm, "end": v(-114.3, 471.42) * mm, "construction": true});
            skLineSegment(sketch, "E355.0.9", {"start": v(-114.3, 471.42) * mm, "end": v(-368.3, 471.42) * mm, "construction": true});
            skLineSegment(sketch, "E355.0.10", {"start": v(-368.3, 471.42) * mm, "end": v(-368.3, 457.2) * mm, "construction": true});
            skLineSegment(sketch, "E355.0.11", {"start": v(-368.3, 457.2) * mm, "end": v(-254, 457.2) * mm, "construction": true});
            skArc(sketch, "E355.0.12", {"start": v(-254, 457.2) * mm, "mid": v(-249.5, 455.34) * mm, "end": v(-247.65, 450.85) * mm, "construction": true});
            skLineSegment(sketch, "E355.0.13", {"start": v(-247.65, 450.85) * mm, "end": v(-247.65, 238) * mm, "construction": true});
            skArc(sketch, "E355.0.14", {"start": v(-247.65, 238) * mm, "mid": v(-249.5, 233.5) * mm, "end": v(-254, 231.65) * mm, "construction": true});
            skLineSegment(sketch, "E355.0.15", {"start": v(-254, 231.65) * mm, "end": v(-368.3, 231.65) * mm, "construction": true});
            skLineSegment(sketch, "E356.bottom", {"start": v(-368.3, 464.31) * mm, "end": v(-114.3, 464.31) * mm});
            skLineSegment(sketch, "E356.top", {"start": v(-368.3, 224.54) * mm, "end": v(-114.3, 224.54) * mm});
            skLineSegment(sketch, "E356.left", {"start": v(-368.3, 464.31) * mm, "end": v(-368.3, 224.54) * mm});
            skLineSegment(sketch, "E356.right", {"start": v(-114.3, 464.31) * mm, "end": v(-114.3, 224.54) * mm});
            skLineSegment(sketch, "E357", {"start": v(-368.3, 344.42) * mm, "end": v(-114.3, 344.42) * mm, "construction": true});
            skLineSegment(sketch, "E358.0", {"start": v(-368.3, 424.42) * mm, "end": v(-114.3, 424.42) * mm, "construction": true});
            skLineSegment(sketch, "E359.0", {"start": v(-318.3, 464.31) * mm, "end": v(-318.3, 224.54) * mm, "construction": true});
            skLineSegment(sketch, "E360.MirrorCS", {"start": v(-368.3, 264.42) * mm, "end": v(-114.3, 264.42) * mm, "construction": true});
            skCircle(sketch, "E361", {"center": v(-318.3, 424.42) * mm, "radius": 10 * mm});
            skCircle(sketch, "E362", {"center": v(-318.3, 344.42) * mm, "radius": 10 * mm});
            skCircle(sketch, "E363", {"center": v(-318.3, 264.42) * mm, "radius": 10 * mm});
            skLineSegment(sketch, "E364", {"start": v(-241.3, 471.42) * mm, "end": v(-241.3, 217.42) * mm, "construction": true});
            skCircle(sketch, "E365.MirrorC", {"center": v(-164.3, 264.42) * mm, "radius": 10 * mm});
            skCircle(sketch, "E366.MirrorC", {"center": v(-164.3, 424.42) * mm, "radius": 10 * mm});
            skCircle(sketch, "E367.MirrorC", {"center": v(-164.3, 344.42) * mm, "radius": 10 * mm});
            skSolve(sketch);
        }
        {
            var Q0;
            Q0=qSketchRegion(id+"F31",true);
            extrude(context, id + "F32", {"entities" : qUnion([Q0]), "depth" : 19 * mm});
        }
        {
            var Q0;
            Q0=makeQuery(id+"F32.opExtrude","CAP_FACE",FACE,{"disambiguationData":[OSD([sQuery(id+"F31.wireOp",EDGE,"E356.bottom"),sQuery(id+"F31.wireOp",EDGE,"E356.top"),sQuery(id+"F31.wireOp",EDGE,"E356.left"),sQuery(id+"F31.wireOp",EDGE,"E356.right"),sQuery(id+"F31.wireOp",EDGE,"E361"),sQuery(id+"F31.wireOp",EDGE,"E362"),sQuery(id+"F31.wireOp",EDGE,"E363"),sQuery(id+"F31.wireOp",EDGE,"E365.MirrorC"),sQuery(id+"F31.wireOp",EDGE,"E366.MirrorC"),sQuery(id+"F31.wireOp",EDGE,"E367.MirrorC")])],"isStart":false});
            var sketch = newSketch(context, id + "F33", { "sketchPlane" : qUnion([Q0])});
            skLineSegment(sketch, "E368.0.0", {"start": v(-114.3, 464.31) * mm, "end": v(-368.3, 464.31) * mm});
            skLineSegment(sketch, "E368.0.1", {"start": v(-368.3, 464.31) * mm, "end": v(-368.3, 224.54) * mm});
            skLineSegment(sketch, "E368.0.2", {"start": v(-368.3, 224.54) * mm, "end": v(-114.3, 224.54) * mm});
            skLineSegment(sketch, "E368.0.3", {"start": v(-114.3, 224.54) * mm, "end": v(-114.3, 464.31) * mm});
            skCircle(sketch, "E369.0", {"center": v(-318.3, 424.42) * mm, "radius": 10 * mm});
            skCircle(sketch, "E370.0", {"center": v(-318.3, 344.42) * mm, "radius": 10 * mm});
            skCircle(sketch, "E371.0", {"center": v(-318.3, 264.42) * mm, "radius": 10 * mm});
            skCircle(sketch, "E372.0", {"center": v(-164.3, 264.42) * mm, "radius": 10 * mm});
            skCircle(sketch, "E373.0", {"center": v(-164.3, 344.42) * mm, "radius": 10 * mm});
            skCircle(sketch, "E374.0", {"center": v(-164.3, 424.42) * mm, "radius": 10 * mm});
            skSolve(sketch);
        }
        {
            var Q0;
            Q0=qSketchRegion(id+"F33",true);
            extrude(context, id + "F34", {"entities" : qUnion([Q0]), "depth" : 19 * mm});
        }
        {
            var Q0;
            Q0=qCreatedBy(id+"F30.planeOp",FACE);
            var sketch = newSketch(context, id + "F35", { "sketchPlane" : qUnion([Q0])});
            skLineSegment(sketch, "E375.0", {"start": v(948.9, 560.42) * mm, "end": v(1098.9, 560.42) * mm, "construction": true});
            skLineSegment(sketch, "E376.0", {"start": v(2973.9, 560.42) * mm, "end": v(3123.9, 560.42) * mm, "construction": true});
            skLineSegment(sketch, "E377.0", {"start": v(3648.9, 560.42) * mm, "end": v(3798.9, 560.42) * mm, "construction": true});
            skLineSegment(sketch, "E378.0", {"start": v(2730.4, 464.31) * mm, "end": v(2730.4, 224.54) * mm, "construction": true});
            skLineSegment(sketch, "E379", {"start": v(948.9, 560.42) * mm, "end": v(3798.9, 560.42) * mm});
            skLineSegment(sketch, "E380.0", {"start": v(1130.3, 509.47) * mm, "end": v(1206.5, 509.47) * mm, "construction": true});
            skLineSegment(sketch, "E381", {"start": v(3798.9, 560.42) * mm, "end": v(3798.9, 224.54) * mm});
            skLineSegment(sketch, "E382", {"start": v(3798.9, 224.54) * mm, "end": v(2730.4, 224.54) * mm});
            skLineSegment(sketch, "E383", {"start": v(948.9, 560.42) * mm, "end": v(948.9, 509.47) * mm});
            skLineSegment(sketch, "E384", {"start": v(948.9, 509.47) * mm, "end": v(2720.4, 509.47) * mm});
            skLineSegment(sketch, "E385", {"start": v(2730.4, 499.47) * mm, "end": v(2730.4, 464.31) * mm});
            skLineSegment(sketch, "E386", {"start": v(2730.4, 464.31) * mm, "end": v(2730.4, 224.54) * mm});
            skPoint(sketch, "E387.visualSharp", {"position": v(2730.4, 509.47) * mm});
            skArc(sketch, "E387.filletArc", {"start": v(2730.4, 499.47) * mm, "mid": v(2727.47, 506.55) * mm, "end": v(2720.4, 509.47) * mm});
            skSolve(sketch);
        }
        {
            var Q0;
            Q0=qSketchRegion(id+"F35",true);
            extrude(context, id + "F36", {"entities" : qUnion([Q0]), "endBound" : BoundingType.SYMMETRIC, "depth" : 12.5 * mm});
        }
        {
            var Q0;
            Q0=makeQuery(id+"F26.opExtrude","SWEPT_FACE",FACE,{"disambiguationData":[OSD([sQuery(id+"F25.wireOp",EDGE,"E336.0.1")])]});
            var sketch = newSketch(context, id + "F37", { "sketchPlane" : qUnion([Q0])});
            skLineSegment(sketch, "E388.0.0", {"start": v(3798.9, 560.42) * mm, "end": v(948.9, 560.42) * mm});
            skLineSegment(sketch, "E388.0.1", {"start": v(948.9, 560.42) * mm, "end": v(948.9, 509.47) * mm});
            skLineSegment(sketch, "E388.0.2", {"start": v(948.9, 509.47) * mm, "end": v(2720.4, 509.47) * mm});
            skArc(sketch, "E388.0.3", {"start": v(2720.4, 509.47) * mm, "mid": v(2727.47, 506.55) * mm, "end": v(2730.4, 499.47) * mm});
            skLineSegment(sketch, "E388.0.4", {"start": v(2730.4, 499.47) * mm, "end": v(2730.4, 224.54) * mm});
            skLineSegment(sketch, "E388.0.5", {"start": v(2730.4, 224.54) * mm, "end": v(3798.9, 224.54) * mm});
            skLineSegment(sketch, "E388.0.6", {"start": v(3798.9, 224.54) * mm, "end": v(3798.9, 560.42) * mm});
            skSolve(sketch);
        }
        {
            var Q0;
            Q0=qSketchRegion(id+"F37",true);
            extrude(context, id + "F38", {"entities" : qUnion([Q0]), "endBound" : BoundingType.SYMMETRIC, "depth" : 12.5 * mm});
        }
        {
            var Q0;
            Q0=makeQuery(id+"F36.opExtrude","SWEPT_EDGE",EDGE,{"disambiguationData":[OSD([sQuery(id+"F35.wireOp",EDGE,"E381"),sQuery(id+"F35.wireOp",EDGE,"E382")])]});
            var Q1;
            Q1=makeQuery(id+"F38.opExtrude","SWEPT_EDGE",EDGE,{"disambiguationData":[OSD([sQuery(id+"F37.wireOp",EDGE,"E388.0.5"),sQuery(id+"F37.wireOp",EDGE,"E388.0.6")])]});
            chamfer(context, id + "F39", {"entities" : qUnion([Q0, Q1]), "chamferType" : ChamferType.TWO_OFFSETS, "width1" : 300 * mm, "oppositeDirection" : false, "width2" : 600 * mm, "tangentPropagation" : true});
        }
        {
            var Q0;
            Q0=makeQuery(id+"F38.opExtrude","SWEPT_BODY",BODY,{"disambiguationData":[OSD([sQuery(id+"F37.wireOp",EDGE,"E388.0.0"),sQuery(id+"F37.wireOp",EDGE,"E388.0.1"),sQuery(id+"F37.wireOp",EDGE,"E388.0.2"),sQuery(id+"F37.wireOp",EDGE,"E388.0.3"),sQuery(id+"F37.wireOp",EDGE,"E388.0.4"),sQuery(id+"F37.wireOp",EDGE,"E388.0.5"),sQuery(id+"F37.wireOp",EDGE,"E388.0.6")])]});
            var Q1;
            Q1=qCreatedBy(id+"F30.planeOp",FACE);
            mirror(context, id + "F40", {"entities" : qUnion([Q0]), "mirrorPlane" : qUnion([Q1])});
        }
        {
            var Q0;
            Q0=makeQuery(id+"F36.opExtrude","SWEPT_EDGE",EDGE,{"disambiguationData":[OSD([sQuery(id+"F35.wireOp",EDGE,"E383"),sQuery(id+"F35.wireOp",EDGE,"E384")])]});
            var Q1;
            Q1=makeQuery(id+"F40.opPattern","COPY",EDGE,{"derivedFrom":makeQuery(id+"F38.opExtrude","SWEPT_EDGE",EDGE,{"disambiguationData":[OSD([sQuery(id+"F37.wireOp",EDGE,"E388.0.1"),sQuery(id+"F37.wireOp",EDGE,"E388.0.2")])]}),"instanceName":"1"});
            var Q2;
            Q2=makeQuery(id+"F38.opExtrude","SWEPT_EDGE",EDGE,{"disambiguationData":[OSD([sQuery(id+"F37.wireOp",EDGE,"E388.0.1"),sQuery(id+"F37.wireOp",EDGE,"E388.0.2")])]});
            chamfer(context, id + "F41", {"entities" : qUnion([Q0, Q1, Q2]), "width" : 40 * mm, "tangentPropagation" : true});
        }
        {
            var Q0;
            Q0=makeQuery(id+"F38.opExtrude","SWEPT_BODY",BODY,{"disambiguationData":[OSD([sQuery(id+"F37.wireOp",EDGE,"E388.0.0"),sQuery(id+"F37.wireOp",EDGE,"E388.0.1"),sQuery(id+"F37.wireOp",EDGE,"E388.0.2"),sQuery(id+"F37.wireOp",EDGE,"E388.0.3"),sQuery(id+"F37.wireOp",EDGE,"E388.0.4"),sQuery(id+"F37.wireOp",EDGE,"E388.0.5"),sQuery(id+"F37.wireOp",EDGE,"E388.0.6")])]});
            var Q1;
            Q1=makeQuery(id+"F34.opExtrude","SWEPT_BODY",BODY,{"disambiguationData":[OSD([sQuery(id+"F33.wireOp",EDGE,"E368.0.0"),sQuery(id+"F33.wireOp",EDGE,"E368.0.1"),sQuery(id+"F33.wireOp",EDGE,"E368.0.2"),sQuery(id+"F33.wireOp",EDGE,"E368.0.3"),sQuery(id+"F33.wireOp",EDGE,"E369.0"),sQuery(id+"F33.wireOp",EDGE,"E370.0"),sQuery(id+"F33.wireOp",EDGE,"E371.0"),sQuery(id+"F33.wireOp",EDGE,"E372.0"),sQuery(id+"F33.wireOp",EDGE,"E373.0"),sQuery(id+"F33.wireOp",EDGE,"E374.0")])]});
            var Q2;
            Q2=makeQuery(id+"F29.opExtrude","SWEPT_BODY",BODY,{"disambiguationData":[OSD([sQuery(id+"F28.wireOp",EDGE,"E354.1.4.0"),sQuery(id+"F28.wireOp",EDGE,"E354.4.4.0"),sQuery(id+"F28.wireOp",EDGE,"E354.7.4.0"),sQuery(id+"F28.wireOp",EDGE,"E354.10.4.0"),sQuery(id+"F28.wireOp",EDGE,"E354.13.4.0"),sQuery(id+"F28.wireOp",EDGE,"E354.15.4.0")])]});
            var Q3;
            Q3=makeQuery(id+"F29.opExtrude","SWEPT_BODY",BODY,{"disambiguationData":[OSD([sQuery(id+"F28.wireOp",EDGE,"E354.1.3.0"),sQuery(id+"F28.wireOp",EDGE,"E354.4.3.0"),sQuery(id+"F28.wireOp",EDGE,"E354.7.3.0"),sQuery(id+"F28.wireOp",EDGE,"E354.10.3.0"),sQuery(id+"F28.wireOp",EDGE,"E354.13.3.0"),sQuery(id+"F28.wireOp",EDGE,"E354.15.3.0")])]});
            var Q4;
            Q4=makeQuery(id+"F29.opExtrude","SWEPT_BODY",BODY,{"disambiguationData":[OSD([sQuery(id+"F28.wireOp",EDGE,"E353.2.0.1"),sQuery(id+"F28.wireOp",EDGE,"E353.2.0.2"),sQuery(id+"F28.wireOp",EDGE,"E353.2.0.3"),sQuery(id+"F28.wireOp",EDGE,"E353.2.0.4"),sQuery(id+"F28.wireOp",EDGE,"E353.2.0.5"),sQuery(id+"F28.wireOp",EDGE,"E353.2.0.6")])]});
            var Q5;
            Q5=makeQuery(id+"F29.opExtrude","SWEPT_BODY",BODY,{"disambiguationData":[OSD([sQuery(id+"F28.wireOp",EDGE,"E353.1.0.1"),sQuery(id+"F28.wireOp",EDGE,"E353.1.0.2"),sQuery(id+"F28.wireOp",EDGE,"E353.1.0.3"),sQuery(id+"F28.wireOp",EDGE,"E353.1.0.4"),sQuery(id+"F28.wireOp",EDGE,"E353.1.0.5"),sQuery(id+"F28.wireOp",EDGE,"E353.1.0.6")])]});
            var Q6;
            Q6=makeQuery(id+"F29.opExtrude","SWEPT_BODY",BODY,{"disambiguationData":[OSD([sQuery(id+"F28.wireOp",EDGE,"E349.bottom"),sQuery(id+"F28.wireOp",EDGE,"E349.top"),sQuery(id+"F28.wireOp",EDGE,"E349.left"),sQuery(id+"F28.wireOp",EDGE,"E349.right"),sQuery(id+"F28.wireOp",EDGE,"E351"),sQuery(id+"F28.wireOp",EDGE,"E352.MirrorC")])]});
            var Q7;
            Q7=makeQuery(id+"F36.opExtrude","SWEPT_BODY",BODY,{"disambiguationData":[OSD([sQuery(id+"F35.wireOp",EDGE,"E379"),sQuery(id+"F35.wireOp",EDGE,"E381"),sQuery(id+"F35.wireOp",EDGE,"E382"),sQuery(id+"F35.wireOp",EDGE,"E383"),sQuery(id+"F35.wireOp",EDGE,"E384"),sQuery(id+"F35.wireOp",EDGE,"E385"),sQuery(id+"F35.wireOp",EDGE,"E386"),sQuery(id+"F35.wireOp",EDGE,"E387.filletArc")])]});
            var Q8;
            Q8=makeQuery(id+"F40.opPattern","COPY",BODY,{"derivedFrom":makeQuery(id+"F38.opExtrude","SWEPT_BODY",BODY,{"disambiguationData":[OSD([sQuery(id+"F37.wireOp",EDGE,"E388.0.0"),sQuery(id+"F37.wireOp",EDGE,"E388.0.1"),sQuery(id+"F37.wireOp",EDGE,"E388.0.2"),sQuery(id+"F37.wireOp",EDGE,"E388.0.3"),sQuery(id+"F37.wireOp",EDGE,"E388.0.4"),sQuery(id+"F37.wireOp",EDGE,"E388.0.5"),sQuery(id+"F37.wireOp",EDGE,"E388.0.6")])]}),"instanceName":"1"});
            var Q9;
            Q9=makeQuery(id+"F26.opExtrude","SWEPT_BODY",BODY,{"disambiguationData":[OSD([sQuery(id+"F25.wireOp",EDGE,"E336.0.0"),sQuery(id+"F25.wireOp",EDGE,"E336.0.1"),sQuery(id+"F25.wireOp",EDGE,"E336.0.2"),sQuery(id+"F25.wireOp",EDGE,"E336.0.3"),sQuery(id+"F25.wireOp",EDGE,"E337.0"),sQuery(id+"F25.wireOp",EDGE,"E338.0")])]});
            var Q10;
            Q10=makeQuery(id+"F26.opExtrude","SWEPT_BODY",BODY,{"disambiguationData":[OSD([sQuery(id+"F25.wireOp",EDGE,"E339.0.0"),sQuery(id+"F25.wireOp",EDGE,"E339.0.1"),sQuery(id+"F25.wireOp",EDGE,"E339.0.2"),sQuery(id+"F25.wireOp",EDGE,"E339.0.3"),sQuery(id+"F25.wireOp",EDGE,"E340.0"),sQuery(id+"F25.wireOp",EDGE,"E341.0")])]});
            booleanBodies(context, id + "F42", {"operationType" : BooleanOperationType.UNION, "tools" : qUnion([Q0, Q1, Q2, Q3, Q4, Q5, Q6, Q7, Q8, Q9, Q10])});
        }
        {
            var Q0;
            {var subQ0=makeQuery(id+"F38.opExtrude","SWEPT_FACE",FACE,{"disambiguationData":[OSD([sQuery(id+"F37.wireOp",EDGE,"E388.0.5")])]});Q0=makeQuery(id+"F42.opBoolean","MERGE",FACE,{"derivedFrom":[makeQuery(id+"F34.opExtrude","SWEPT_FACE",FACE,{"disambiguationData":[OSD([sQuery(id+"F33.wireOp",EDGE,"E368.0.2")])]}),makeQuery(id+"F36.opExtrude","SWEPT_FACE",FACE,{"disambiguationData":[OSD([sQuery(id+"F35.wireOp",EDGE,"E382")])]}),subQ0,makeQuery(id+"F40.opPattern","COPY",FACE,{"derivedFrom":subQ0,"instanceName":"1"})]});}
            var sketch = newSketch(context, id + "F43", { "sketchPlane" : qUnion([Q0])});
            skLineSegment(sketch, "E389.0.0", {"start": v(2730.4, 349.35) * mm, "end": v(3198.9, 349.35) * mm, "construction": true});
            skLineSegment(sketch, "E389.0.1", {"start": v(3198.9, 349.35) * mm, "end": v(3198.9, 361.85) * mm, "construction": true});
            skLineSegment(sketch, "E389.0.2", {"start": v(3198.9, 361.85) * mm, "end": v(2730.4, 361.85) * mm, "construction": true});
            skLineSegment(sketch, "E389.0.3", {"start": v(2730.4, 361.85) * mm, "end": v(2730.4, 368.3) * mm, "construction": true});
            skLineSegment(sketch, "E389.0.4", {"start": v(2730.4, 368.3) * mm, "end": v(2711.4, 368.3) * mm, "construction": true});
            skLineSegment(sketch, "E389.0.5", {"start": v(2711.4, 368.3) * mm, "end": v(2711.4, 114.3) * mm, "construction": true});
            skLineSegment(sketch, "E389.0.6", {"start": v(2711.4, 114.3) * mm, "end": v(2730.4, 114.3) * mm, "construction": true});
            skLineSegment(sketch, "E389.0.7", {"start": v(2730.4, 114.3) * mm, "end": v(2730.4, 120.75) * mm, "construction": true});
            skLineSegment(sketch, "E389.0.8", {"start": v(2730.4, 120.75) * mm, "end": v(3198.9, 120.75) * mm, "construction": true});
            skLineSegment(sketch, "E389.0.9", {"start": v(3198.9, 120.75) * mm, "end": v(3198.9, 133.25) * mm, "construction": true});
            skLineSegment(sketch, "E389.0.10", {"start": v(3198.9, 133.25) * mm, "end": v(2730.4, 133.25) * mm, "construction": true});
            skLineSegment(sketch, "E389.0.11", {"start": v(2730.4, 133.25) * mm, "end": v(2730.4, 235.05) * mm, "construction": true});
            skLineSegment(sketch, "E389.0.12", {"start": v(2730.4, 235.05) * mm, "end": v(3198.9, 235.05) * mm, "construction": true});
            skLineSegment(sketch, "E389.0.13", {"start": v(3198.9, 235.05) * mm, "end": v(3198.9, 247.55) * mm, "construction": true});
            skLineSegment(sketch, "E389.0.14", {"start": v(3198.9, 247.55) * mm, "end": v(2730.4, 247.55) * mm, "construction": true});
            skLineSegment(sketch, "E389.0.15", {"start": v(2730.4, 247.55) * mm, "end": v(2730.4, 349.35) * mm, "construction": true});
            skPoint(sketch, "E390.oppositeSnap0", {"position": v(3198.9, 127) * mm});
            skLineSegment(sketch, "E390.bottom", {"start": v(3198.9, 355.6) * mm, "end": v(3048.9, 355.6) * mm});
            skLineSegment(sketch, "E390.top", {"start": v(3198.9, 127) * mm, "end": v(3048.9, 127) * mm});
            skLineSegment(sketch, "E390.left", {"start": v(3198.9, 355.6) * mm, "end": v(3198.9, 127) * mm});
            skLineSegment(sketch, "E390.right", {"start": v(3048.9, 355.6) * mm, "end": v(3048.9, 127) * mm});
            skSolve(sketch);
        }
        {
            var Q0;
            Q0=qSketchRegion(id+"F43",true);
            extrude(context, id + "F44", {"entities" : qUnion([Q0]), "operationType" : NewBodyOperationType.ADD, "depth" : 12.5 * mm});
        }
    });
